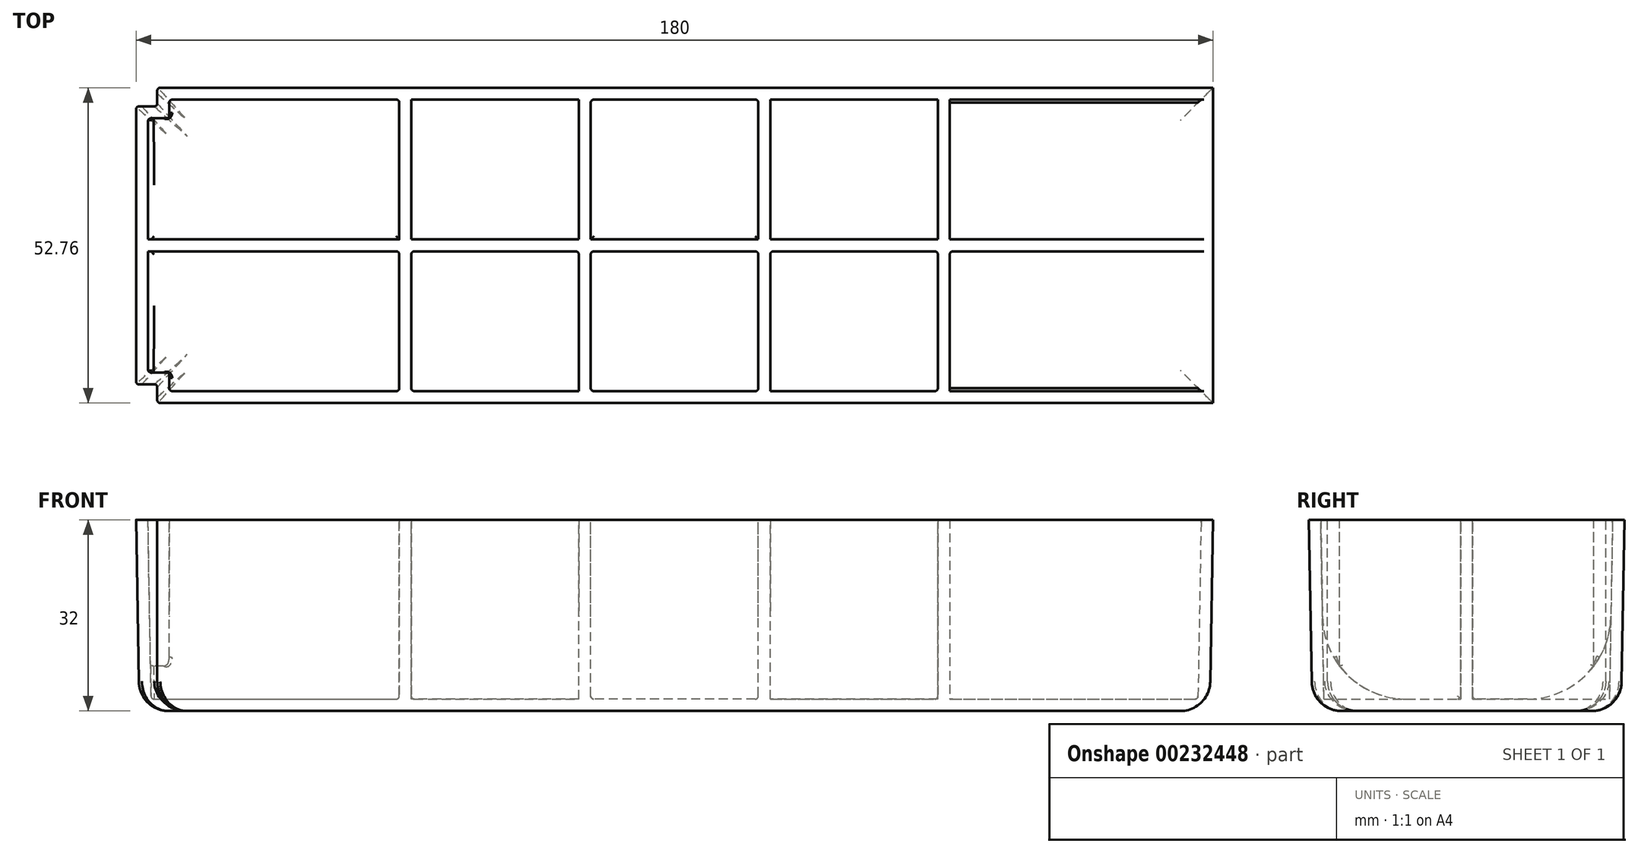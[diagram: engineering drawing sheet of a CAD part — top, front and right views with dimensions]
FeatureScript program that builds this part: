
annotation { "Feature Type Name" : "Feature", "Feature Type Description" : "" }
export const myFeature = defineFeature(function(context is Context, id is Id, definition is map)
    precondition{}
    {
        {
            var Q0;
            Q0=qCreatedBy(makeId("Top.planeOp"),FACE);
            var sketch = newSketch(context, id + "F0", { "sketchPlane" : qUnion([Q0])});
            skLineSegment(sketch, "E0.bottom", {"start": v(90, 26.38) * mm, "end": v(-90, 26.38) * mm});
            skLineSegment(sketch, "E0.top", {"start": v(90, -26.38) * mm, "end": v(-90, -26.38) * mm});
            skLineSegment(sketch, "E0.left", {"start": v(90, 26.38) * mm, "end": v(90, -26.38) * mm});
            skLineSegment(sketch, "E0.right", {"start": v(-90, 26.38) * mm, "end": v(-90, -26.38) * mm});
            skPoint(sketch, "E0.middle", {"position": v(0, 0) * mm});
            skSolve(sketch);
        }
        {
            var Q0;
            Q0=makeQuery(id+"F0.imprint","IMPRINT",FACE,{"disambiguationData":[TD([[makeQuery(id+"F0.imprint","IMPRINT",EDGE,{"derivedFrom":sQuery(id+"F0.wireOp",EDGE,"E0.bottom")}),1.0]])]});
            extrude(context, id + "F1", {"entities" : qUnion([Q0]), "oppositeDirection" : true, "depth" : 32 * mm, "hasDraft" : true, "draftAngle" : 1 * degree, "draftPullDirection" : true});
        }
        {
            var Q0;
            Q0=makeQuery(id+"F1.opExtrude","CAP_FACE",FACE,{"disambiguationData":[OSD([sQuery(id+"F0.wireOp",EDGE,"E0.bottom"),sQuery(id+"F0.wireOp",EDGE,"E0.top"),sQuery(id+"F0.wireOp",EDGE,"E0.left"),sQuery(id+"F0.wireOp",EDGE,"E0.right")])],"isStart":true});
            var sketch = newSketch(context, id + "F2", { "sketchPlane" : qUnion([Q0])});
            skLineSegment(sketch, "E1.bottom", {"start": v(-90, 23.25) * mm, "end": v(90, 23.25) * mm});
            skLineSegment(sketch, "E1.top", {"start": v(-90, -23.25) * mm, "end": v(90, -23.25) * mm});
            skLineSegment(sketch, "E1.left", {"start": v(-90, 23.25) * mm, "end": v(-90, -23.25) * mm});
            skLineSegment(sketch, "E1.right", {"start": v(90, 23.25) * mm, "end": v(90, -23.25) * mm});
            skPoint(sketch, "E1.middle", {"position": v(0, 0) * mm});
            skLineSegment(sketch, "E2.bottom", {"start": v(-86.45, 31.86) * mm, "end": v(-112.75, 31.86) * mm});
            skLineSegment(sketch, "E2.top", {"start": v(-86.45, -31.86) * mm, "end": v(-112.75, -31.86) * mm});
            skLineSegment(sketch, "E2.left", {"start": v(-86.45, 31.86) * mm, "end": v(-86.45, -31.86) * mm});
            skLineSegment(sketch, "E2.right", {"start": v(-112.75, 31.86) * mm, "end": v(-112.75, -31.86) * mm});
            skPoint(sketch, "E2.middle", {"position": v(-99.6, 0) * mm});
            skLineSegment(sketch, "E3.0", {"start": v(-90, 26.38) * mm, "end": v(-90, -26.38) * mm, "construction": true});
            skSolve(sketch);
        }
        {
            var Q0;
            {var subQ0=sQuery(id+"F2.wireOp",EDGE,"E1.bottom");var subQ3=sQuery(id+"F2.wireOp",EDGE,"E2.left");var subQ4=makeQuery(id+"F2.imprint","INTERSECT",VERTEX,{"derivedFrom":[subQ0,subQ3]});Q0=makeQuery(id+"F2.imprint","IMPRINT",FACE,{"disambiguationData":[TD([[makeQuery(id+"F2.imprint","IMPRINT",EDGE,{"disambiguationData":[TD([[subQ4,1.0]])],"derivedFrom":subQ3}),-1.0]])]});}
            var Q1;
            {var subQ0=sQuery(id+"F2.wireOp",EDGE,"E1.top");var subQ3=sQuery(id+"F2.wireOp",EDGE,"E2.left");var subQ4=makeQuery(id+"F2.imprint","INTERSECT",VERTEX,{"derivedFrom":[subQ0,subQ3]});Q1=makeQuery(id+"F2.imprint","IMPRINT",FACE,{"disambiguationData":[TD([[makeQuery(id+"F2.imprint","IMPRINT",EDGE,{"disambiguationData":[TD([[subQ4,-1.0]])],"derivedFrom":subQ3}),-1.0]])]});}
            extrude(context, id + "F3", {"entities" : qUnion([Q0, Q1]), "operationType" : NewBodyOperationType.REMOVE, "endBound" : BoundingType.THROUGH_ALL, "oppositeDirection" : true, "depth" : 25 * mm});
        }
        {
            var Q0;
            Q0=makeQuery(id+"F1.opExtrude","CAP_FACE",FACE,{"disambiguationData":[OSD([sQuery(id+"F0.wireOp",EDGE,"E0.bottom"),sQuery(id+"F0.wireOp",EDGE,"E0.top"),sQuery(id+"F0.wireOp",EDGE,"E0.left"),sQuery(id+"F0.wireOp",EDGE,"E0.right")])],"isStart":true});
            shell(context, id + "F4", {"entities" : qUnion([Q0]), "thickness" : 2 * mm});
        }
        {
            var Q0;
            Q0=makeQuery(id+"F1.opExtrude","CAP_FACE",FACE,{"disambiguationData":[OSD([sQuery(id+"F0.wireOp",EDGE,"E0.bottom"),sQuery(id+"F0.wireOp",EDGE,"E0.top"),sQuery(id+"F0.wireOp",EDGE,"E0.left"),sQuery(id+"F0.wireOp",EDGE,"E0.right")])],"isStart":false});
            fillet(context, id + "F5", {"entities" : qUnion([Q0]), "radius" : 5 * mm, "tangentPropagation" : true, "allowEdgeOverflow" : false});
        }
        {
            var Q0;
            Q0=makeQuery(id+"F1.opExtrude","CAP_FACE",FACE,{"disambiguationData":[OSD([sQuery(id+"F0.wireOp",EDGE,"E0.bottom"),sQuery(id+"F0.wireOp",EDGE,"E0.top"),sQuery(id+"F0.wireOp",EDGE,"E0.left"),sQuery(id+"F0.wireOp",EDGE,"E0.right")])],"isStart":true});
            var sketch = newSketch(context, id + "F6", { "sketchPlane" : qUnion([Q0])});
            skLineSegment(sketch, "E4", {"start": v(0, 26.38) * mm, "end": v(0, -26.38) * mm, "construction": true});
            skLineSegment(sketch, "E5.1.0.0", {"start": v(15, 26.38) * mm, "end": v(15, -26.38) * mm, "construction": true});
            skLineSegment(sketch, "E5.direction1", {"start": v(0, -26.38) * mm, "end": v(15, -26.38) * mm, "construction": true});
            skLineSegment(sketch, "E6", {"start": v(-15, 26.38) * mm, "end": v(-15, -26.38) * mm, "construction": true});
            skLineSegment(sketch, "E7.bottom", {"start": v(16, 26.38) * mm, "end": v(14, 26.38) * mm});
            skLineSegment(sketch, "E7.top", {"start": v(16, -26.38) * mm, "end": v(14, -26.38) * mm});
            skLineSegment(sketch, "E7.left", {"start": v(16, 26.38) * mm, "end": v(16, -26.38) * mm});
            skLineSegment(sketch, "E7.right", {"start": v(14, 26.38) * mm, "end": v(14, -26.38) * mm});
            skPoint(sketch, "E7.middle", {"position": v(15, 0) * mm});
            skLineSegment(sketch, "E8.bottom", {"start": v(90, -1) * mm, "end": v(-90, -1) * mm});
            skLineSegment(sketch, "E8.top", {"start": v(90, 1) * mm, "end": v(-90, 1) * mm});
            skLineSegment(sketch, "E8.left", {"start": v(90, -1) * mm, "end": v(90, 1) * mm});
            skLineSegment(sketch, "E8.right", {"start": v(-90, -1) * mm, "end": v(-90, 1) * mm});
            skPoint(sketch, "E8.middle", {"position": v(0, 0) * mm});
            skLineSegment(sketch, "E9.bottom", {"start": v(-14, 26.38) * mm, "end": v(-16, 26.38) * mm});
            skLineSegment(sketch, "E9.top", {"start": v(-14, -26.38) * mm, "end": v(-16, -26.38) * mm});
            skLineSegment(sketch, "E9.left", {"start": v(-14, 26.38) * mm, "end": v(-14, -26.38) * mm});
            skLineSegment(sketch, "E9.right", {"start": v(-16, 26.38) * mm, "end": v(-16, -26.38) * mm});
            skPoint(sketch, "E9.middle", {"position": v(-15, 0) * mm});
            skLineSegment(sketch, "E10", {"start": v(-45, 26.38) * mm, "end": v(-45, -26.38) * mm, "construction": true});
            skLineSegment(sketch, "E11", {"start": v(45, 26.38) * mm, "end": v(45, -26.38) * mm, "construction": true});
            skLineSegment(sketch, "E12.bottom", {"start": v(-44, 26.38) * mm, "end": v(-46, 26.38) * mm});
            skLineSegment(sketch, "E12.top", {"start": v(-44, -26.38) * mm, "end": v(-46, -26.38) * mm});
            skLineSegment(sketch, "E12.left", {"start": v(-44, 26.38) * mm, "end": v(-44, -26.38) * mm});
            skLineSegment(sketch, "E12.right", {"start": v(-46, 26.38) * mm, "end": v(-46, -26.38) * mm});
            skPoint(sketch, "E12.middle", {"position": v(-45, 0) * mm});
            skLineSegment(sketch, "E13.bottom", {"start": v(46, 26.38) * mm, "end": v(44, 26.38) * mm});
            skLineSegment(sketch, "E13.top", {"start": v(46, -26.38) * mm, "end": v(44, -26.38) * mm});
            skLineSegment(sketch, "E13.left", {"start": v(46, 26.38) * mm, "end": v(46, -26.38) * mm});
            skLineSegment(sketch, "E13.right", {"start": v(44, 26.38) * mm, "end": v(44, -26.38) * mm});
            skPoint(sketch, "E13.middle", {"position": v(45, 0) * mm});
            skSolve(sketch);
        }
        {
            var Q0;
            {var subQ0=sQuery(id+"F6.wireOp",EDGE,"E9.right");var subQ1=sQuery(id+"F6.wireOp",EDGE,"E8.bottom");var subQ2=makeQuery(id+"F6.imprint","INTERSECT",VERTEX,{"derivedFrom":[subQ1,subQ0]});Q0=makeQuery(id+"F6.imprint","IMPRINT",FACE,{"disambiguationData":[TD([[makeQuery(id+"F6.imprint","IMPRINT",EDGE,{"disambiguationData":[TD([[subQ2,1.0]])],"derivedFrom":subQ0}),-1.0]])]});}
            var Q1;
            {var subQ0=sQuery(id+"F6.wireOp",EDGE,"E9.left");var subQ1=sQuery(id+"F6.wireOp",EDGE,"E8.bottom");var subQ2=makeQuery(id+"F6.imprint","INTERSECT",VERTEX,{"derivedFrom":[subQ1,subQ0]});Q1=makeQuery(id+"F6.imprint","IMPRINT",FACE,{"disambiguationData":[TD([[makeQuery(id+"F6.imprint","IMPRINT",EDGE,{"disambiguationData":[TD([[subQ2,-1.0]])],"derivedFrom":subQ1}),1.0]])]});}
            var Q2;
            {var subQ0=sQuery(id+"F6.wireOp",EDGE,"E9.left");var subQ1=sQuery(id+"F6.wireOp",EDGE,"E8.bottom");var subQ2=makeQuery(id+"F6.imprint","INTERSECT",VERTEX,{"derivedFrom":[subQ1,subQ0]});Q2=makeQuery(id+"F6.imprint","IMPRINT",FACE,{"disambiguationData":[TD([[makeQuery(id+"F6.imprint","IMPRINT",EDGE,{"disambiguationData":[TD([[subQ2,-1.0]])],"derivedFrom":subQ1}),-1.0]])]});}
            var Q3;
            {var subQ0=sQuery(id+"F6.wireOp",EDGE,"E9.left");var subQ1=sQuery(id+"F6.wireOp",EDGE,"E8.top");var subQ2=makeQuery(id+"F6.imprint","INTERSECT",VERTEX,{"derivedFrom":[subQ1,subQ0]});Q3=makeQuery(id+"F6.imprint","IMPRINT",FACE,{"disambiguationData":[TD([[makeQuery(id+"F6.imprint","IMPRINT",EDGE,{"disambiguationData":[TD([[subQ2,-1.0]])],"derivedFrom":subQ1}),-1.0]])]});}
            var Q4;
            {var subQ0=sQuery(id+"F6.wireOp",EDGE,"E8.top");var subQ1=sQuery(id+"F6.wireOp",EDGE,"E7.right");var subQ2=makeQuery(id+"F6.imprint","INTERSECT",VERTEX,{"derivedFrom":[subQ1,subQ0]});Q4=makeQuery(id+"F6.imprint","IMPRINT",FACE,{"disambiguationData":[TD([[makeQuery(id+"F6.imprint","IMPRINT",EDGE,{"disambiguationData":[TD([[subQ2,-1.0]])],"derivedFrom":subQ1}),-1.0]])]});}
            var Q5;
            {var subQ0=sQuery(id+"F6.wireOp",EDGE,"E8.top");var subQ1=sQuery(id+"F6.wireOp",EDGE,"E7.left");var subQ2=makeQuery(id+"F6.imprint","INTERSECT",VERTEX,{"derivedFrom":[subQ1,subQ0]});Q5=makeQuery(id+"F6.imprint","IMPRINT",FACE,{"disambiguationData":[TD([[makeQuery(id+"F6.imprint","IMPRINT",EDGE,{"disambiguationData":[TD([[subQ2,-1.0]])],"derivedFrom":subQ1}),1.0]])]});}
            var Q6;
            {var subQ0=sQuery(id+"F6.wireOp",EDGE,"E8.top");var subQ1=sQuery(id+"F6.wireOp",EDGE,"E7.left");var subQ2=makeQuery(id+"F6.imprint","INTERSECT",VERTEX,{"derivedFrom":[subQ1,subQ0]});Q6=makeQuery(id+"F6.imprint","IMPRINT",FACE,{"disambiguationData":[TD([[makeQuery(id+"F6.imprint","IMPRINT",EDGE,{"disambiguationData":[TD([[subQ2,-1.0]])],"derivedFrom":subQ1}),-1.0]])]});}
            var Q7;
            {var subQ0=sQuery(id+"F6.wireOp",EDGE,"E8.bottom");var subQ1=sQuery(id+"F6.wireOp",EDGE,"E7.left");var subQ2=makeQuery(id+"F6.imprint","INTERSECT",VERTEX,{"derivedFrom":[subQ1,subQ0]});Q7=makeQuery(id+"F6.imprint","IMPRINT",FACE,{"disambiguationData":[TD([[makeQuery(id+"F6.imprint","IMPRINT",EDGE,{"disambiguationData":[TD([[subQ2,-1.0]])],"derivedFrom":subQ0}),1.0]])]});}
            var Q8;
            {var subQ0=sQuery(id+"F6.wireOp",EDGE,"E8.top");var subQ1=sQuery(id+"F6.wireOp",EDGE,"E7.left");var subQ2=makeQuery(id+"F6.imprint","INTERSECT",VERTEX,{"derivedFrom":[subQ1,subQ0]});Q8=makeQuery(id+"F6.imprint","IMPRINT",FACE,{"disambiguationData":[TD([[makeQuery(id+"F6.imprint","IMPRINT",EDGE,{"disambiguationData":[TD([[subQ2,-1.0]])],"derivedFrom":subQ0}),-1.0]])]});}
            var Q9;
            {var subQ0=sQuery(id+"F6.wireOp",EDGE,"E12.right");var subQ1=sQuery(id+"F6.wireOp",EDGE,"E8.bottom");var subQ2=makeQuery(id+"F6.imprint","INTERSECT",VERTEX,{"derivedFrom":[subQ1,subQ0]});Q9=makeQuery(id+"F6.imprint","IMPRINT",FACE,{"disambiguationData":[TD([[makeQuery(id+"F6.imprint","IMPRINT",EDGE,{"disambiguationData":[TD([[subQ2,1.0]])],"derivedFrom":subQ0}),-1.0]])]});}
            var Q10;
            {var subQ0=sQuery(id+"F6.wireOp",EDGE,"E12.left");var subQ1=sQuery(id+"F6.wireOp",EDGE,"E8.bottom");var subQ2=makeQuery(id+"F6.imprint","INTERSECT",VERTEX,{"derivedFrom":[subQ1,subQ0]});Q10=makeQuery(id+"F6.imprint","IMPRINT",FACE,{"disambiguationData":[TD([[makeQuery(id+"F6.imprint","IMPRINT",EDGE,{"disambiguationData":[TD([[subQ2,-1.0]])],"derivedFrom":subQ1}),-1.0]])]});}
            var Q11;
            {var subQ0=sQuery(id+"F6.wireOp",EDGE,"E12.left");var subQ1=sQuery(id+"F6.wireOp",EDGE,"E8.top");var subQ2=makeQuery(id+"F6.imprint","INTERSECT",VERTEX,{"derivedFrom":[subQ1,subQ0]});Q11=makeQuery(id+"F6.imprint","IMPRINT",FACE,{"disambiguationData":[TD([[makeQuery(id+"F6.imprint","IMPRINT",EDGE,{"disambiguationData":[TD([[subQ2,-1.0]])],"derivedFrom":subQ1}),-1.0]])]});}
            var Q12;
            {var subQ0=sQuery(id+"F6.wireOp",EDGE,"E12.left");var subQ1=sQuery(id+"F6.wireOp",EDGE,"E8.bottom");var subQ2=makeQuery(id+"F6.imprint","INTERSECT",VERTEX,{"derivedFrom":[subQ1,subQ0]});Q12=makeQuery(id+"F6.imprint","IMPRINT",FACE,{"disambiguationData":[TD([[makeQuery(id+"F6.imprint","IMPRINT",EDGE,{"disambiguationData":[TD([[subQ2,-1.0]])],"derivedFrom":subQ1}),1.0]])]});}
            var Q13;
            {var subQ0=sQuery(id+"F6.wireOp",EDGE,"E13.left");var subQ1=sQuery(id+"F6.wireOp",EDGE,"E8.bottom");var subQ2=makeQuery(id+"F6.imprint","INTERSECT",VERTEX,{"derivedFrom":[subQ1,subQ0]});Q13=makeQuery(id+"F6.imprint","IMPRINT",FACE,{"disambiguationData":[TD([[makeQuery(id+"F6.imprint","IMPRINT",EDGE,{"disambiguationData":[TD([[subQ2,1.0]])],"derivedFrom":subQ0}),1.0]])]});}
            var Q14;
            {var subQ0=sQuery(id+"F6.wireOp",EDGE,"E13.left");var subQ1=sQuery(id+"F6.wireOp",EDGE,"E8.bottom");var subQ2=makeQuery(id+"F6.imprint","INTERSECT",VERTEX,{"derivedFrom":[subQ1,subQ0]});Q14=makeQuery(id+"F6.imprint","IMPRINT",FACE,{"disambiguationData":[TD([[makeQuery(id+"F6.imprint","IMPRINT",EDGE,{"disambiguationData":[TD([[subQ2,-1.0]])],"derivedFrom":subQ1}),-1.0]])]});}
            var Q15;
            {var subQ0=sQuery(id+"F6.wireOp",EDGE,"E13.left");var subQ1=sQuery(id+"F6.wireOp",EDGE,"E8.top");var subQ2=makeQuery(id+"F6.imprint","INTERSECT",VERTEX,{"derivedFrom":[subQ1,subQ0]});Q15=makeQuery(id+"F6.imprint","IMPRINT",FACE,{"disambiguationData":[TD([[makeQuery(id+"F6.imprint","IMPRINT",EDGE,{"disambiguationData":[TD([[subQ2,-1.0]])],"derivedFrom":subQ1}),-1.0]])]});}
            var Q16;
            {var subQ0=sQuery(id+"F6.wireOp",EDGE,"E13.left");var subQ1=sQuery(id+"F6.wireOp",EDGE,"E8.bottom");var subQ2=makeQuery(id+"F6.imprint","INTERSECT",VERTEX,{"derivedFrom":[subQ1,subQ0]});Q16=makeQuery(id+"F6.imprint","IMPRINT",FACE,{"disambiguationData":[TD([[makeQuery(id+"F6.imprint","IMPRINT",EDGE,{"disambiguationData":[TD([[subQ2,-1.0]])],"derivedFrom":subQ1}),1.0]])]});}
            extrude(context, id + "F7", {"entities" : qUnion([Q0, Q1, Q2, Q3, Q4, Q5, Q6, Q7, Q8, Q9, Q10, Q11, Q12, Q13, Q14, Q15, Q16]), "operationType" : NewBodyOperationType.ADD, "endBound" : BoundingType.UP_TO_NEXT, "oppositeDirection" : true, "depth" : 25 * mm});
        }
        {
            var Q0;
            {var subQ0=sQuery(id+"F6.wireOp",EDGE,"E8.bottom");var subQ1=sQuery(id+"F0.wireOp",EDGE,"E0.right");Q0=makeQuery(id+"F7.opExtrude","TWEAK_EDGE",EDGE,{"derivedFrom":[makeQuery(id+"F4.opShell","OFFSET_FACE",FACE,{"disambiguationData":[OSD([sQuery(id+"F0.wireOp",EDGE,"E0.bottom"),sQuery(id+"F0.wireOp",EDGE,"E0.top"),sQuery(id+"F0.wireOp",EDGE,"E0.left"),subQ1])]}),makeQuery(id+"F6.imprint","IMPRINT",EDGE,{"disambiguationData":[TD([[makeQuery(id+"F6.imprint","INTERSECT",VERTEX,{"derivedFrom":[subQ0,sQuery(id+"F6.wireOp",EDGE,"E9.right")]}),-1.0]])],"derivedFrom":subQ0})]});}
            var Q1;
            {var subQ0=sQuery(id+"F6.wireOp",EDGE,"E8.bottom");Q1=makeQuery(id+"F7.opExtrude","TWEAK_EDGE",EDGE,{"derivedFrom":[makeQuery(id+"F4.opShell","OFFSET_FACE",FACE,{"disambiguationData":[OSD([sQuery(id+"F0.wireOp",EDGE,"E0.bottom"),sQuery(id+"F0.wireOp",EDGE,"E0.top"),sQuery(id+"F0.wireOp",EDGE,"E0.left"),sQuery(id+"F0.wireOp",EDGE,"E0.right")])]}),makeQuery(id+"F6.imprint","IMPRINT",EDGE,{"disambiguationData":[TD([[makeQuery(id+"F6.imprint","INTERSECT",VERTEX,{"derivedFrom":[sQuery(id+"F6.wireOp",EDGE,"E7.right"),subQ0]}),-1.0]])],"derivedFrom":subQ0})]});}
            var Q2;
            {var subQ0=sQuery(id+"F6.wireOp",EDGE,"E8.bottom");var subQ1=sQuery(id+"F0.wireOp",EDGE,"E0.left");Q2=makeQuery(id+"F7.opExtrude","TWEAK_EDGE",EDGE,{"derivedFrom":[makeQuery(id+"F4.opShell","OFFSET_FACE",FACE,{"disambiguationData":[OSD([sQuery(id+"F0.wireOp",EDGE,"E0.bottom"),sQuery(id+"F0.wireOp",EDGE,"E0.top"),subQ1,sQuery(id+"F0.wireOp",EDGE,"E0.right")])]}),makeQuery(id+"F6.imprint","IMPRINT",EDGE,{"disambiguationData":[TD([[makeQuery(id+"F6.imprint","INTERSECT",VERTEX,{"derivedFrom":[sQuery(id+"F6.wireOp",EDGE,"E7.left"),subQ0]}),1.0]])],"derivedFrom":subQ0})]});}
            var Q3;
            {var subQ0=sQuery(id+"F6.wireOp",EDGE,"E8.top");var subQ1=sQuery(id+"F0.wireOp",EDGE,"E0.left");Q3=makeQuery(id+"F7.opExtrude","TWEAK_EDGE",EDGE,{"derivedFrom":[makeQuery(id+"F4.opShell","OFFSET_FACE",FACE,{"disambiguationData":[OSD([sQuery(id+"F0.wireOp",EDGE,"E0.bottom"),sQuery(id+"F0.wireOp",EDGE,"E0.top"),subQ1,sQuery(id+"F0.wireOp",EDGE,"E0.right")])]}),makeQuery(id+"F6.imprint","IMPRINT",EDGE,{"disambiguationData":[TD([[makeQuery(id+"F6.imprint","INTERSECT",VERTEX,{"derivedFrom":[sQuery(id+"F6.wireOp",EDGE,"E7.left"),subQ0]}),1.0]])],"derivedFrom":subQ0})]});}
            var Q4;
            {var subQ0=sQuery(id+"F6.wireOp",EDGE,"E8.top");Q4=makeQuery(id+"F7.opExtrude","TWEAK_EDGE",EDGE,{"derivedFrom":[makeQuery(id+"F4.opShell","OFFSET_FACE",FACE,{"disambiguationData":[OSD([sQuery(id+"F0.wireOp",EDGE,"E0.bottom"),sQuery(id+"F0.wireOp",EDGE,"E0.top"),sQuery(id+"F0.wireOp",EDGE,"E0.left"),sQuery(id+"F0.wireOp",EDGE,"E0.right")])]}),makeQuery(id+"F6.imprint","IMPRINT",EDGE,{"disambiguationData":[TD([[makeQuery(id+"F6.imprint","INTERSECT",VERTEX,{"derivedFrom":[sQuery(id+"F6.wireOp",EDGE,"E7.right"),subQ0]}),-1.0]])],"derivedFrom":subQ0})]});}
            var Q5;
            {var subQ0=sQuery(id+"F6.wireOp",EDGE,"E8.top");var subQ1=sQuery(id+"F0.wireOp",EDGE,"E0.right");Q5=makeQuery(id+"F7.opExtrude","TWEAK_EDGE",EDGE,{"derivedFrom":[makeQuery(id+"F4.opShell","OFFSET_FACE",FACE,{"disambiguationData":[OSD([sQuery(id+"F0.wireOp",EDGE,"E0.bottom"),sQuery(id+"F0.wireOp",EDGE,"E0.top"),sQuery(id+"F0.wireOp",EDGE,"E0.left"),subQ1])]}),makeQuery(id+"F6.imprint","IMPRINT",EDGE,{"disambiguationData":[TD([[makeQuery(id+"F6.imprint","INTERSECT",VERTEX,{"derivedFrom":[subQ0,sQuery(id+"F6.wireOp",EDGE,"E9.right")]}),-1.0]])],"derivedFrom":subQ0})]});}
            var Q6;
            {var subQ0=sQuery(id+"F6.wireOp",EDGE,"E8.top");var subQ1=sQuery(id+"F0.wireOp",EDGE,"E0.right");Q6=makeQuery(id+"F7.opExtrude","TWEAK_EDGE",EDGE,{"derivedFrom":[makeQuery(id+"F4.opShell","OFFSET_FACE",FACE,{"disambiguationData":[OSD([sQuery(id+"F0.wireOp",EDGE,"E0.bottom"),sQuery(id+"F0.wireOp",EDGE,"E0.top"),sQuery(id+"F0.wireOp",EDGE,"E0.left"),subQ1])]}),makeQuery(id+"F6.imprint","IMPRINT",EDGE,{"disambiguationData":[TD([[makeQuery(id+"F6.imprint","INTERSECT",VERTEX,{"derivedFrom":[subQ0,sQuery(id+"F6.wireOp",EDGE,"E12.right")]}),-1.0]])],"derivedFrom":subQ0})]});}
            var Q7;
            {var subQ0=sQuery(id+"F6.wireOp",EDGE,"E8.top");var subQ1=sQuery(id+"F0.wireOp",EDGE,"E0.left");Q7=makeQuery(id+"F7.opExtrude","TWEAK_EDGE",EDGE,{"derivedFrom":[makeQuery(id+"F4.opShell","OFFSET_FACE",FACE,{"disambiguationData":[OSD([sQuery(id+"F0.wireOp",EDGE,"E0.bottom"),sQuery(id+"F0.wireOp",EDGE,"E0.top"),subQ1,sQuery(id+"F0.wireOp",EDGE,"E0.right")])]}),makeQuery(id+"F6.imprint","IMPRINT",EDGE,{"disambiguationData":[TD([[makeQuery(id+"F6.imprint","INTERSECT",VERTEX,{"derivedFrom":[subQ0,sQuery(id+"F6.wireOp",EDGE,"E13.left")]}),1.0]])],"derivedFrom":subQ0})]});}
            var Q8;
            {var subQ0=sQuery(id+"F6.wireOp",EDGE,"E8.bottom");var subQ1=sQuery(id+"F0.wireOp",EDGE,"E0.left");Q8=makeQuery(id+"F7.opExtrude","TWEAK_EDGE",EDGE,{"derivedFrom":[makeQuery(id+"F4.opShell","OFFSET_FACE",FACE,{"disambiguationData":[OSD([sQuery(id+"F0.wireOp",EDGE,"E0.bottom"),sQuery(id+"F0.wireOp",EDGE,"E0.top"),subQ1,sQuery(id+"F0.wireOp",EDGE,"E0.right")])]}),makeQuery(id+"F6.imprint","IMPRINT",EDGE,{"disambiguationData":[TD([[makeQuery(id+"F6.imprint","INTERSECT",VERTEX,{"derivedFrom":[subQ0,sQuery(id+"F6.wireOp",EDGE,"E13.left")]}),1.0]])],"derivedFrom":subQ0})]});}
            var Q9;
            {var subQ0=sQuery(id+"F6.wireOp",EDGE,"E8.bottom");var subQ1=sQuery(id+"F0.wireOp",EDGE,"E0.right");Q9=makeQuery(id+"F7.opExtrude","TWEAK_EDGE",EDGE,{"derivedFrom":[makeQuery(id+"F4.opShell","OFFSET_FACE",FACE,{"disambiguationData":[OSD([sQuery(id+"F0.wireOp",EDGE,"E0.bottom"),sQuery(id+"F0.wireOp",EDGE,"E0.top"),sQuery(id+"F0.wireOp",EDGE,"E0.left"),subQ1])]}),makeQuery(id+"F6.imprint","IMPRINT",EDGE,{"disambiguationData":[TD([[makeQuery(id+"F6.imprint","INTERSECT",VERTEX,{"derivedFrom":[subQ0,sQuery(id+"F6.wireOp",EDGE,"E12.right")]}),-1.0]])],"derivedFrom":subQ0})]});}
            var Q10;
            {var subQ0=sQuery(id+"F2.wireOp",EDGE,"E2.left");var subQ1=sQuery(id+"F0.wireOp",EDGE,"E0.bottom");Q10=makeQuery(id+"F7.boolean.opBoolean","SPLIT",EDGE,{"disambiguationData":[TD([makeQuery(id+"F4.opShell","OFFSET_FACE",FACE,{"disambiguationData":[OSD([subQ0]),TDD([makeQuery(id+"F3.boolean.opBoolean","COPY",FACE,{"derivedFrom":makeQuery(id+"F3.opExtrude","SWEPT_FACE",FACE,{"disambiguationData":[OSD([subQ0]),TDD([makeQuery(id+"F2.imprint","IMPRINT",EDGE,{"disambiguationData":[TD([[makeQuery(id+"F2.imprint","INTERSECT",VERTEX,{"derivedFrom":[sQuery(id+"F2.wireOp",EDGE,"E1.bottom"),subQ0]}),1.0]])],"derivedFrom":subQ0})])]})})])]})])],"derivedFrom":makeQuery(id+"F4.opShell","OFFSET_EDGE",EDGE,{"disambiguationData":[OSD([subQ1]),TDD([makeQuery(id+"F1.opExtrude","CAP_EDGE",EDGE,{"disambiguationData":[OSD([subQ1])],"isStart":false})])]})});}
            var Q11;
            {var subQ0=sQuery(id+"F0.wireOp",EDGE,"E0.bottom");var subQ1=sQuery(id+"F6.wireOp",EDGE,"E9.right");var subQ2=sQuery(id+"F6.wireOp",EDGE,"E8.top");Q11=makeQuery(id+"F7.boolean.opBoolean","SPLIT",EDGE,{"disambiguationData":[TD([makeQuery(id+"F7.opExtrude","SWEPT_FACE",FACE,{"disambiguationData":[OSD([subQ1]),TDD([makeQuery(id+"F6.imprint","IMPRINT",EDGE,{"disambiguationData":[TD([[makeQuery(id+"F6.imprint","INTERSECT",VERTEX,{"derivedFrom":[subQ2,subQ1]}),1.0]])],"derivedFrom":subQ1})])]})])],"derivedFrom":makeQuery(id+"F4.opShell","OFFSET_EDGE",EDGE,{"disambiguationData":[OSD([subQ0]),TDD([makeQuery(id+"F1.opExtrude","CAP_EDGE",EDGE,{"disambiguationData":[OSD([subQ0])],"isStart":false})])]})});}
            var Q12;
            {var subQ0=sQuery(id+"F0.wireOp",EDGE,"E0.bottom");var subQ1=sQuery(id+"F6.wireOp",EDGE,"E8.top");var subQ2=sQuery(id+"F6.wireOp",EDGE,"E7.right");Q12=makeQuery(id+"F7.boolean.opBoolean","SPLIT",EDGE,{"disambiguationData":[TD([makeQuery(id+"F7.opExtrude","SWEPT_FACE",FACE,{"disambiguationData":[OSD([subQ2]),TDD([makeQuery(id+"F6.imprint","IMPRINT",EDGE,{"disambiguationData":[TD([[makeQuery(id+"F6.imprint","INTERSECT",VERTEX,{"derivedFrom":[subQ2,subQ1]}),1.0]])],"derivedFrom":subQ2})])]})])],"derivedFrom":makeQuery(id+"F4.opShell","OFFSET_EDGE",EDGE,{"disambiguationData":[OSD([subQ0]),TDD([makeQuery(id+"F1.opExtrude","CAP_EDGE",EDGE,{"disambiguationData":[OSD([subQ0])],"isStart":false})])]})});}
            var Q13;
            {var subQ0=sQuery(id+"F0.wireOp",EDGE,"E0.bottom");var subQ1=sQuery(id+"F6.wireOp",EDGE,"E8.top");var subQ2=sQuery(id+"F6.wireOp",EDGE,"E7.left");Q13=makeQuery(id+"F7.boolean.opBoolean","SPLIT",EDGE,{"disambiguationData":[TD([makeQuery(id+"F7.opExtrude","SWEPT_FACE",FACE,{"disambiguationData":[OSD([subQ2]),TDD([makeQuery(id+"F6.imprint","IMPRINT",EDGE,{"disambiguationData":[TD([[makeQuery(id+"F6.imprint","INTERSECT",VERTEX,{"derivedFrom":[subQ2,subQ1]}),1.0]])],"derivedFrom":subQ2})])]})])],"derivedFrom":makeQuery(id+"F4.opShell","OFFSET_EDGE",EDGE,{"disambiguationData":[OSD([subQ0]),TDD([makeQuery(id+"F1.opExtrude","CAP_EDGE",EDGE,{"disambiguationData":[OSD([subQ0])],"isStart":false})])]})});}
            var Q14;
            {var subQ0=sQuery(id+"F2.wireOp",EDGE,"E2.left");var subQ1=sQuery(id+"F0.wireOp",EDGE,"E0.bottom");Q14=makeQuery(id+"F7.boolean.opBoolean","SPLIT",EDGE,{"disambiguationData":[TD([makeQuery(id+"F4.opShell","OFFSET_FACE",FACE,{"disambiguationData":[OSD([subQ0]),TDD([makeQuery(id+"Fj79t6Fnd16a4gd_1.1.F3.boolean.opBoolean","COPY",FACE,{"derivedFrom":makeQuery(id+"Fj79t6Fnd16a4gd_1.1.F3.opExtrude","SWEPT_FACE",FACE,{"disambiguationData":[OSD([subQ0]),TDD([makeQuery(id+"F2.imprint","IMPRINT",EDGE,{"disambiguationData":[TD([[makeQuery(id+"F2.imprint","INTERSECT",VERTEX,{"derivedFrom":[sQuery(id+"F2.wireOp",EDGE,"E1.bottom"),subQ0]}),1.0]])],"derivedFrom":subQ0})])]})})])]})])],"derivedFrom":makeQuery(id+"F4.opShell","OFFSET_EDGE",EDGE,{"disambiguationData":[OSD([subQ1]),TDD([makeQuery(id+"F1.opExtrude","CAP_EDGE",EDGE,{"disambiguationData":[OSD([subQ1])],"isStart":false})])]})});}
            var Q15;
            {var subQ0=sQuery(id+"F2.wireOp",EDGE,"E2.left");var subQ1=sQuery(id+"F0.wireOp",EDGE,"E0.top");Q15=makeQuery(id+"F7.boolean.opBoolean","SPLIT",EDGE,{"disambiguationData":[TD([makeQuery(id+"F4.opShell","OFFSET_FACE",FACE,{"disambiguationData":[OSD([subQ0]),TDD([makeQuery(id+"Fj79t6Fnd16a4gd_1.1.F3.boolean.opBoolean","COPY",FACE,{"derivedFrom":makeQuery(id+"Fj79t6Fnd16a4gd_1.1.F3.opExtrude","SWEPT_FACE",FACE,{"disambiguationData":[OSD([subQ0]),TDD([makeQuery(id+"F2.imprint","IMPRINT",EDGE,{"disambiguationData":[TD([[makeQuery(id+"F2.imprint","INTERSECT",VERTEX,{"derivedFrom":[sQuery(id+"F2.wireOp",EDGE,"E1.top"),subQ0]}),-1.0]])],"derivedFrom":subQ0})])]})})])]})])],"derivedFrom":makeQuery(id+"F4.opShell","OFFSET_EDGE",EDGE,{"disambiguationData":[OSD([subQ1]),TDD([makeQuery(id+"F1.opExtrude","CAP_EDGE",EDGE,{"disambiguationData":[OSD([subQ1])],"isStart":false})])]})});}
            var Q16;
            {var subQ0=sQuery(id+"F0.wireOp",EDGE,"E0.top");var subQ1=sQuery(id+"F6.wireOp",EDGE,"E8.bottom");var subQ2=sQuery(id+"F6.wireOp",EDGE,"E7.left");Q16=makeQuery(id+"F7.boolean.opBoolean","SPLIT",EDGE,{"disambiguationData":[TD([makeQuery(id+"F7.opExtrude","SWEPT_FACE",FACE,{"disambiguationData":[OSD([subQ2]),TDD([makeQuery(id+"F6.imprint","IMPRINT",EDGE,{"disambiguationData":[TD([[makeQuery(id+"F6.imprint","INTERSECT",VERTEX,{"derivedFrom":[subQ2,subQ1]}),-1.0]])],"derivedFrom":subQ2})])]})])],"derivedFrom":makeQuery(id+"F4.opShell","OFFSET_EDGE",EDGE,{"disambiguationData":[OSD([subQ0]),TDD([makeQuery(id+"F1.opExtrude","CAP_EDGE",EDGE,{"disambiguationData":[OSD([subQ0])],"isStart":false})])]})});}
            var Q17;
            {var subQ0=sQuery(id+"F0.wireOp",EDGE,"E0.top");var subQ1=sQuery(id+"F6.wireOp",EDGE,"E8.bottom");var subQ2=sQuery(id+"F6.wireOp",EDGE,"E7.right");Q17=makeQuery(id+"F7.boolean.opBoolean","SPLIT",EDGE,{"disambiguationData":[TD([makeQuery(id+"F7.opExtrude","SWEPT_FACE",FACE,{"disambiguationData":[OSD([subQ2]),TDD([makeQuery(id+"F6.imprint","IMPRINT",EDGE,{"disambiguationData":[TD([[makeQuery(id+"F6.imprint","INTERSECT",VERTEX,{"derivedFrom":[subQ2,subQ1]}),-1.0]])],"derivedFrom":subQ2})])]})])],"derivedFrom":makeQuery(id+"F4.opShell","OFFSET_EDGE",EDGE,{"disambiguationData":[OSD([subQ0]),TDD([makeQuery(id+"F1.opExtrude","CAP_EDGE",EDGE,{"disambiguationData":[OSD([subQ0])],"isStart":false})])]})});}
            var Q18;
            {var subQ0=sQuery(id+"F0.wireOp",EDGE,"E0.top");var subQ2=sQuery(id+"F6.wireOp",EDGE,"E8.bottom");var subQ4=sQuery(id+"F6.wireOp",EDGE,"E9.right");Q18=makeQuery(id+"F7.boolean.opBoolean","SPLIT",EDGE,{"disambiguationData":[TD([makeQuery(id+"F7.opExtrude","SWEPT_FACE",FACE,{"disambiguationData":[OSD([subQ4]),TDD([makeQuery(id+"F6.imprint","IMPRINT",EDGE,{"disambiguationData":[TD([[makeQuery(id+"F6.imprint","INTERSECT",VERTEX,{"derivedFrom":[subQ2,subQ4]}),-1.0]])],"derivedFrom":subQ4})])]})])],"derivedFrom":makeQuery(id+"F4.opShell","OFFSET_EDGE",EDGE,{"disambiguationData":[OSD([subQ0]),TDD([makeQuery(id+"F1.opExtrude","CAP_EDGE",EDGE,{"disambiguationData":[OSD([subQ0])],"isStart":false})])]})});}
            var Q19;
            {var subQ0=sQuery(id+"F2.wireOp",EDGE,"E2.left");var subQ1=sQuery(id+"F0.wireOp",EDGE,"E0.top");Q19=makeQuery(id+"F7.boolean.opBoolean","SPLIT",EDGE,{"disambiguationData":[TD([makeQuery(id+"F4.opShell","OFFSET_FACE",FACE,{"disambiguationData":[OSD([subQ0]),TDD([makeQuery(id+"F3.boolean.opBoolean","COPY",FACE,{"derivedFrom":makeQuery(id+"F3.opExtrude","SWEPT_FACE",FACE,{"disambiguationData":[OSD([subQ0]),TDD([makeQuery(id+"F2.imprint","IMPRINT",EDGE,{"disambiguationData":[TD([[makeQuery(id+"F2.imprint","INTERSECT",VERTEX,{"derivedFrom":[sQuery(id+"F2.wireOp",EDGE,"E1.top"),subQ0]}),-1.0]])],"derivedFrom":subQ0})])]})})])]})])],"derivedFrom":makeQuery(id+"F4.opShell","OFFSET_EDGE",EDGE,{"disambiguationData":[OSD([subQ1]),TDD([makeQuery(id+"F1.opExtrude","CAP_EDGE",EDGE,{"disambiguationData":[OSD([subQ1])],"isStart":false})])]})});}
            fillet(context, id + "F8", {"entities" : qUnion([Q0, Q1, Q2, Q3, Q4, Q5, Q6, Q7, Q8, Q9, Q10, Q11, Q12, Q13, Q14, Q15, Q16, Q17, Q18, Q19]), "radius" : 14 * mm, "tangentPropagation" : true, "allowEdgeOverflow" : false});
        }
        {
            var Q0;
            {var subQ0=sQuery(id+"F2.wireOp",EDGE,"E2.left");var subQ1=sQuery(id+"F0.wireOp",EDGE,"E0.bottom");Q0=makeQuery(id+"F3.boolean.opBoolean","INTERSECT",EDGE,{"derivedFrom":[makeQuery(id+"F1.opExtrude","SWEPT_FACE",FACE,{"disambiguationData":[OSD([subQ1])]}),makeQuery(id+"F3.opExtrude","SWEPT_FACE",FACE,{"disambiguationData":[OSD([subQ0]),TDD([makeQuery(id+"F2.imprint","IMPRINT",EDGE,{"disambiguationData":[TD([[makeQuery(id+"F2.imprint","INTERSECT",VERTEX,{"derivedFrom":[sQuery(id+"F2.wireOp",EDGE,"E1.bottom"),subQ0]}),1.0]])],"derivedFrom":subQ0})])]})]});}
            var Q1;
            Q1=makeQuery(id+"F3.boolean.opBoolean","COPY",EDGE,{"derivedFrom":makeQuery(id+"F3.opExtrude","SWEPT_EDGE",EDGE,{"disambiguationData":[OSD([sQuery(id+"F2.wireOp",EDGE,"E1.bottom"),sQuery(id+"F2.wireOp",EDGE,"E2.left")])]})});
            var Q2;
            Q2=makeQuery(id+"F3.boolean.opBoolean","INTERSECT",EDGE,{"derivedFrom":[makeQuery(id+"F1.opExtrude","SWEPT_FACE",FACE,{"disambiguationData":[OSD([sQuery(id+"F0.wireOp",EDGE,"E0.right")])]}),makeQuery(id+"F3.opExtrude","SWEPT_FACE",FACE,{"disambiguationData":[OSD([sQuery(id+"F2.wireOp",EDGE,"E1.bottom")])]})]});
            var Q3;
            {var subQ0=sQuery(id+"F2.wireOp",EDGE,"E2.left");var subQ1=sQuery(id+"F0.wireOp",EDGE,"E0.top");Q3=makeQuery(id+"F3.boolean.opBoolean","INTERSECT",EDGE,{"derivedFrom":[makeQuery(id+"F1.opExtrude","SWEPT_FACE",FACE,{"disambiguationData":[OSD([subQ1])]}),makeQuery(id+"F3.opExtrude","SWEPT_FACE",FACE,{"disambiguationData":[OSD([subQ0]),TDD([makeQuery(id+"F2.imprint","IMPRINT",EDGE,{"disambiguationData":[TD([[makeQuery(id+"F2.imprint","INTERSECT",VERTEX,{"derivedFrom":[sQuery(id+"F2.wireOp",EDGE,"E1.top"),subQ0]}),-1.0]])],"derivedFrom":subQ0})])]})]});}
            var Q4;
            Q4=makeQuery(id+"F3.boolean.opBoolean","INTERSECT",EDGE,{"derivedFrom":[makeQuery(id+"F1.opExtrude","SWEPT_FACE",FACE,{"disambiguationData":[OSD([sQuery(id+"F0.wireOp",EDGE,"E0.right")])]}),makeQuery(id+"F3.opExtrude","SWEPT_FACE",FACE,{"disambiguationData":[OSD([sQuery(id+"F2.wireOp",EDGE,"E1.top")])]})]});
            var Q5;
            Q5=makeQuery(id+"F3.boolean.opBoolean","COPY",EDGE,{"derivedFrom":makeQuery(id+"F3.opExtrude","SWEPT_EDGE",EDGE,{"disambiguationData":[OSD([sQuery(id+"F2.wireOp",EDGE,"E1.top"),sQuery(id+"F2.wireOp",EDGE,"E2.left")])]})});
            var Q6;
            Q6=makeQuery(id+"Fj79t6Fnd16a4gd_1.1.F3.boolean.opBoolean","INTERSECT",EDGE,{"derivedFrom":[makeQuery(id+"F1.opExtrude","SWEPT_FACE",FACE,{"disambiguationData":[OSD([sQuery(id+"F0.wireOp",EDGE,"E0.left")])]}),makeQuery(id+"Fj79t6Fnd16a4gd_1.1.F3.opExtrude","SWEPT_FACE",FACE,{"disambiguationData":[OSD([sQuery(id+"F2.wireOp",EDGE,"E1.top")])]})]});
            var Q7;
            Q7=makeQuery(id+"Fj79t6Fnd16a4gd_1.1.F3.boolean.opBoolean","COPY",EDGE,{"derivedFrom":makeQuery(id+"Fj79t6Fnd16a4gd_1.1.F3.opExtrude","SWEPT_EDGE",EDGE,{"disambiguationData":[OSD([sQuery(id+"F2.wireOp",EDGE,"E1.top"),sQuery(id+"F2.wireOp",EDGE,"E2.left")])]})});
            var Q8;
            {var subQ0=sQuery(id+"F2.wireOp",EDGE,"E2.left");var subQ1=sQuery(id+"F0.wireOp",EDGE,"E0.top");Q8=makeQuery(id+"Fj79t6Fnd16a4gd_1.1.F3.boolean.opBoolean","INTERSECT",EDGE,{"derivedFrom":[makeQuery(id+"F1.opExtrude","SWEPT_FACE",FACE,{"disambiguationData":[OSD([subQ1])]}),makeQuery(id+"Fj79t6Fnd16a4gd_1.1.F3.opExtrude","SWEPT_FACE",FACE,{"disambiguationData":[OSD([subQ0]),TDD([makeQuery(id+"F2.imprint","IMPRINT",EDGE,{"disambiguationData":[TD([[makeQuery(id+"F2.imprint","INTERSECT",VERTEX,{"derivedFrom":[sQuery(id+"F2.wireOp",EDGE,"E1.top"),subQ0]}),-1.0]])],"derivedFrom":subQ0})])]})]});}
            var Q9;
            {var subQ0=sQuery(id+"F2.wireOp",EDGE,"E2.left");var subQ1=sQuery(id+"F0.wireOp",EDGE,"E0.bottom");Q9=makeQuery(id+"Fj79t6Fnd16a4gd_1.1.F3.boolean.opBoolean","INTERSECT",EDGE,{"derivedFrom":[makeQuery(id+"F1.opExtrude","SWEPT_FACE",FACE,{"disambiguationData":[OSD([subQ1])]}),makeQuery(id+"Fj79t6Fnd16a4gd_1.1.F3.opExtrude","SWEPT_FACE",FACE,{"disambiguationData":[OSD([subQ0]),TDD([makeQuery(id+"F2.imprint","IMPRINT",EDGE,{"disambiguationData":[TD([[makeQuery(id+"F2.imprint","INTERSECT",VERTEX,{"derivedFrom":[sQuery(id+"F2.wireOp",EDGE,"E1.bottom"),subQ0]}),1.0]])],"derivedFrom":subQ0})])]})]});}
            var Q10;
            Q10=makeQuery(id+"Fj79t6Fnd16a4gd_1.1.F3.boolean.opBoolean","COPY",EDGE,{"derivedFrom":makeQuery(id+"Fj79t6Fnd16a4gd_1.1.F3.opExtrude","SWEPT_EDGE",EDGE,{"disambiguationData":[OSD([sQuery(id+"F2.wireOp",EDGE,"E1.bottom"),sQuery(id+"F2.wireOp",EDGE,"E2.left")])]})});
            var Q11;
            Q11=makeQuery(id+"Fj79t6Fnd16a4gd_1.1.F3.boolean.opBoolean","INTERSECT",EDGE,{"derivedFrom":[makeQuery(id+"F1.opExtrude","SWEPT_FACE",FACE,{"disambiguationData":[OSD([sQuery(id+"F0.wireOp",EDGE,"E0.left")])]}),makeQuery(id+"Fj79t6Fnd16a4gd_1.1.F3.opExtrude","SWEPT_FACE",FACE,{"disambiguationData":[OSD([sQuery(id+"F2.wireOp",EDGE,"E1.bottom")])]})]});
            var Q12;
            {var subQ0=sQuery(id+"F2.wireOp",EDGE,"E2.left");var subQ1=sQuery(id+"F0.wireOp",EDGE,"E0.bottom");Q12=makeQuery(id+"F4.opShell","OFFSET_EDGE",EDGE,{"disambiguationData":[OSD([subQ1,subQ0]),TDD([makeQuery(id+"F3.boolean.opBoolean","INTERSECT",EDGE,{"derivedFrom":[makeQuery(id+"F1.opExtrude","SWEPT_FACE",FACE,{"disambiguationData":[OSD([subQ1])]}),makeQuery(id+"F3.opExtrude","SWEPT_FACE",FACE,{"disambiguationData":[OSD([subQ0]),TDD([makeQuery(id+"F2.imprint","IMPRINT",EDGE,{"disambiguationData":[TD([[makeQuery(id+"F2.imprint","INTERSECT",VERTEX,{"derivedFrom":[sQuery(id+"F2.wireOp",EDGE,"E1.bottom"),subQ0]}),1.0]])],"derivedFrom":subQ0})])]})]})])]});}
            var Q13;
            {var subQ0=sQuery(id+"F2.wireOp",EDGE,"E2.left");var subQ1=sQuery(id+"F2.wireOp",EDGE,"E1.bottom");Q13=makeQuery(id+"F4.opShell","OFFSET_EDGE",EDGE,{"disambiguationData":[OSD([subQ1,subQ0]),TDD([makeQuery(id+"F3.boolean.opBoolean","COPY",EDGE,{"derivedFrom":makeQuery(id+"F3.opExtrude","SWEPT_EDGE",EDGE,{"disambiguationData":[OSD([subQ1,subQ0])]})})])]});}
            var Q14;
            Q14=makeQuery(id+"F4.opShell","OFFSET_EDGE",EDGE,{"disambiguationData":[OSD([sQuery(id+"F0.wireOp",EDGE,"E0.right"),sQuery(id+"F2.wireOp",EDGE,"E1.bottom")])]});
            var Q15;
            {var subQ0=sQuery(id+"F2.wireOp",EDGE,"E2.left");var subQ1=sQuery(id+"F0.wireOp",EDGE,"E0.bottom");Q15=makeQuery(id+"F4.opShell","OFFSET_EDGE",EDGE,{"disambiguationData":[OSD([subQ1,subQ0]),TDD([makeQuery(id+"Fj79t6Fnd16a4gd_1.1.F3.boolean.opBoolean","INTERSECT",EDGE,{"derivedFrom":[makeQuery(id+"F1.opExtrude","SWEPT_FACE",FACE,{"disambiguationData":[OSD([subQ1])]}),makeQuery(id+"Fj79t6Fnd16a4gd_1.1.F3.opExtrude","SWEPT_FACE",FACE,{"disambiguationData":[OSD([subQ0]),TDD([makeQuery(id+"F2.imprint","IMPRINT",EDGE,{"disambiguationData":[TD([[makeQuery(id+"F2.imprint","INTERSECT",VERTEX,{"derivedFrom":[sQuery(id+"F2.wireOp",EDGE,"E1.bottom"),subQ0]}),1.0]])],"derivedFrom":subQ0})])]})]})])]});}
            var Q16;
            {var subQ0=sQuery(id+"F2.wireOp",EDGE,"E2.left");var subQ1=sQuery(id+"F2.wireOp",EDGE,"E1.bottom");Q16=makeQuery(id+"F4.opShell","OFFSET_EDGE",EDGE,{"disambiguationData":[OSD([subQ1,subQ0]),TDD([makeQuery(id+"Fj79t6Fnd16a4gd_1.1.F3.boolean.opBoolean","COPY",EDGE,{"derivedFrom":makeQuery(id+"Fj79t6Fnd16a4gd_1.1.F3.opExtrude","SWEPT_EDGE",EDGE,{"disambiguationData":[OSD([subQ1,subQ0])]})})])]});}
            var Q17;
            Q17=makeQuery(id+"F4.opShell","OFFSET_EDGE",EDGE,{"disambiguationData":[OSD([sQuery(id+"F0.wireOp",EDGE,"E0.left"),sQuery(id+"F2.wireOp",EDGE,"E1.bottom")])]});
            var Q18;
            Q18=makeQuery(id+"F4.opShell","OFFSET_EDGE",EDGE,{"disambiguationData":[OSD([sQuery(id+"F0.wireOp",EDGE,"E0.left"),sQuery(id+"F2.wireOp",EDGE,"E1.top")])]});
            var Q19;
            {var subQ0=sQuery(id+"F2.wireOp",EDGE,"E2.left");var subQ1=sQuery(id+"F2.wireOp",EDGE,"E1.top");Q19=makeQuery(id+"F4.opShell","OFFSET_EDGE",EDGE,{"disambiguationData":[OSD([subQ1,subQ0]),TDD([makeQuery(id+"Fj79t6Fnd16a4gd_1.1.F3.boolean.opBoolean","COPY",EDGE,{"derivedFrom":makeQuery(id+"Fj79t6Fnd16a4gd_1.1.F3.opExtrude","SWEPT_EDGE",EDGE,{"disambiguationData":[OSD([subQ1,subQ0])]})})])]});}
            var Q20;
            {var subQ0=sQuery(id+"F2.wireOp",EDGE,"E2.left");var subQ1=sQuery(id+"F0.wireOp",EDGE,"E0.top");Q20=makeQuery(id+"F4.opShell","OFFSET_EDGE",EDGE,{"disambiguationData":[OSD([subQ1,subQ0]),TDD([makeQuery(id+"Fj79t6Fnd16a4gd_1.1.F3.boolean.opBoolean","INTERSECT",EDGE,{"derivedFrom":[makeQuery(id+"F1.opExtrude","SWEPT_FACE",FACE,{"disambiguationData":[OSD([subQ1])]}),makeQuery(id+"Fj79t6Fnd16a4gd_1.1.F3.opExtrude","SWEPT_FACE",FACE,{"disambiguationData":[OSD([subQ0]),TDD([makeQuery(id+"F2.imprint","IMPRINT",EDGE,{"disambiguationData":[TD([[makeQuery(id+"F2.imprint","INTERSECT",VERTEX,{"derivedFrom":[sQuery(id+"F2.wireOp",EDGE,"E1.top"),subQ0]}),-1.0]])],"derivedFrom":subQ0})])]})]})])]});}
            var Q21;
            Q21=makeQuery(id+"F4.opShell","OFFSET_EDGE",EDGE,{"disambiguationData":[OSD([sQuery(id+"F0.wireOp",EDGE,"E0.right"),sQuery(id+"F2.wireOp",EDGE,"E1.top")])]});
            var Q22;
            {var subQ0=sQuery(id+"F2.wireOp",EDGE,"E2.left");var subQ1=sQuery(id+"F2.wireOp",EDGE,"E1.top");Q22=makeQuery(id+"F4.opShell","OFFSET_EDGE",EDGE,{"disambiguationData":[OSD([subQ1,subQ0]),TDD([makeQuery(id+"F3.boolean.opBoolean","COPY",EDGE,{"derivedFrom":makeQuery(id+"F3.opExtrude","SWEPT_EDGE",EDGE,{"disambiguationData":[OSD([subQ1,subQ0])]})})])]});}
            var Q23;
            {var subQ0=sQuery(id+"F2.wireOp",EDGE,"E2.left");var subQ1=sQuery(id+"F0.wireOp",EDGE,"E0.top");Q23=makeQuery(id+"F4.opShell","OFFSET_EDGE",EDGE,{"disambiguationData":[OSD([subQ1,subQ0]),TDD([makeQuery(id+"F3.boolean.opBoolean","INTERSECT",EDGE,{"derivedFrom":[makeQuery(id+"F1.opExtrude","SWEPT_FACE",FACE,{"disambiguationData":[OSD([subQ1])]}),makeQuery(id+"F3.opExtrude","SWEPT_FACE",FACE,{"disambiguationData":[OSD([subQ0]),TDD([makeQuery(id+"F2.imprint","IMPRINT",EDGE,{"disambiguationData":[TD([[makeQuery(id+"F2.imprint","INTERSECT",VERTEX,{"derivedFrom":[sQuery(id+"F2.wireOp",EDGE,"E1.top"),subQ0]}),-1.0]])],"derivedFrom":subQ0})])]})]})])]});}
            var Q24;
            {var subQ0=sQuery(id+"F0.wireOp",EDGE,"E0.bottom");var subQ2=sQuery(id+"F2.wireOp",EDGE,"E1.bottom");var subQ4=sQuery(id+"F0.wireOp",EDGE,"E0.right");Q24=makeQuery(id+"F7.boolean.opBoolean","SPLIT",FACE,{"disambiguationData":[TD([makeQuery(id+"F4.opShell","OFFSET_FACE",FACE,{"disambiguationData":[OSD([subQ2]),TDD([makeQuery(id+"F3.boolean.opBoolean","COPY",FACE,{"derivedFrom":makeQuery(id+"F3.opExtrude","SWEPT_FACE",FACE,{"disambiguationData":[OSD([subQ2])]})})])]})])],"derivedFrom":makeQuery(id+"F4.opShell","OFFSET_FACE",FACE,{"disambiguationData":[OSD([subQ0,sQuery(id+"F0.wireOp",EDGE,"E0.top"),sQuery(id+"F0.wireOp",EDGE,"E0.left"),subQ4])]})});}
            var Q25;
            {var subQ0=sQuery(id+"F0.wireOp",EDGE,"E0.bottom");var subQ1=sQuery(id+"F6.wireOp",EDGE,"E8.top");var subQ2=sQuery(id+"F6.wireOp",EDGE,"E7.right");var subQ3=makeQuery(id+"F6.imprint","INTERSECT",VERTEX,{"derivedFrom":[subQ2,subQ1]});Q25=makeQuery(id+"F7.boolean.opBoolean","SPLIT",FACE,{"disambiguationData":[TD([makeQuery(id+"F7.opExtrude","SWEPT_FACE",FACE,{"disambiguationData":[OSD([subQ1]),TDD([makeQuery(id+"F6.imprint","IMPRINT",EDGE,{"disambiguationData":[TD([[subQ3,-1.0]])],"derivedFrom":subQ1})])]})])],"derivedFrom":makeQuery(id+"F4.opShell","OFFSET_FACE",FACE,{"disambiguationData":[OSD([subQ0,sQuery(id+"F0.wireOp",EDGE,"E0.top"),sQuery(id+"F0.wireOp",EDGE,"E0.left"),sQuery(id+"F0.wireOp",EDGE,"E0.right")])]})});}
            var Q26;
            {var subQ0=sQuery(id+"F0.wireOp",EDGE,"E0.bottom");var subQ1=sQuery(id+"F0.wireOp",EDGE,"E0.left");var subQ6=sQuery(id+"F2.wireOp",EDGE,"E1.bottom");Q26=makeQuery(id+"F7.boolean.opBoolean","SPLIT",FACE,{"disambiguationData":[TD([makeQuery(id+"F4.opShell","OFFSET_FACE",FACE,{"disambiguationData":[OSD([subQ6]),TDD([makeQuery(id+"Fj79t6Fnd16a4gd_1.1.F3.boolean.opBoolean","COPY",FACE,{"derivedFrom":makeQuery(id+"Fj79t6Fnd16a4gd_1.1.F3.opExtrude","SWEPT_FACE",FACE,{"disambiguationData":[OSD([subQ6])]})})])]})])],"derivedFrom":makeQuery(id+"F4.opShell","OFFSET_FACE",FACE,{"disambiguationData":[OSD([subQ0,sQuery(id+"F0.wireOp",EDGE,"E0.top"),subQ1,sQuery(id+"F0.wireOp",EDGE,"E0.right")])]})});}
            var Q27;
            {var subQ0=sQuery(id+"F0.wireOp",EDGE,"E0.top");var subQ1=sQuery(id+"F0.wireOp",EDGE,"E0.left");var subQ3=sQuery(id+"F2.wireOp",EDGE,"E1.top");Q27=makeQuery(id+"F7.boolean.opBoolean","SPLIT",FACE,{"disambiguationData":[TD([makeQuery(id+"F4.opShell","OFFSET_FACE",FACE,{"disambiguationData":[OSD([subQ3]),TDD([makeQuery(id+"Fj79t6Fnd16a4gd_1.1.F3.boolean.opBoolean","COPY",FACE,{"derivedFrom":makeQuery(id+"Fj79t6Fnd16a4gd_1.1.F3.opExtrude","SWEPT_FACE",FACE,{"disambiguationData":[OSD([subQ3])]})})])]})])],"derivedFrom":makeQuery(id+"F4.opShell","OFFSET_FACE",FACE,{"disambiguationData":[OSD([sQuery(id+"F0.wireOp",EDGE,"E0.bottom"),subQ0,subQ1,sQuery(id+"F0.wireOp",EDGE,"E0.right")])]})});}
            var Q28;
            {var subQ0=sQuery(id+"F0.wireOp",EDGE,"E0.top");var subQ1=sQuery(id+"F6.wireOp",EDGE,"E8.bottom");var subQ2=sQuery(id+"F6.wireOp",EDGE,"E7.right");var subQ3=makeQuery(id+"F6.imprint","INTERSECT",VERTEX,{"derivedFrom":[subQ2,subQ1]});Q28=makeQuery(id+"F7.boolean.opBoolean","SPLIT",FACE,{"disambiguationData":[TD([makeQuery(id+"F7.opExtrude","SWEPT_FACE",FACE,{"disambiguationData":[OSD([subQ1]),TDD([makeQuery(id+"F6.imprint","IMPRINT",EDGE,{"disambiguationData":[TD([[subQ3,-1.0]])],"derivedFrom":subQ1})])]})])],"derivedFrom":makeQuery(id+"F4.opShell","OFFSET_FACE",FACE,{"disambiguationData":[OSD([sQuery(id+"F0.wireOp",EDGE,"E0.bottom"),subQ0,sQuery(id+"F0.wireOp",EDGE,"E0.left"),sQuery(id+"F0.wireOp",EDGE,"E0.right")])]})});}
            var Q29;
            {var subQ0=sQuery(id+"F0.wireOp",EDGE,"E0.top");var subQ5=sQuery(id+"F0.wireOp",EDGE,"E0.right");var subQ7=sQuery(id+"F2.wireOp",EDGE,"E1.top");Q29=makeQuery(id+"F7.boolean.opBoolean","SPLIT",FACE,{"disambiguationData":[TD([makeQuery(id+"F4.opShell","OFFSET_FACE",FACE,{"disambiguationData":[OSD([subQ7]),TDD([makeQuery(id+"F3.boolean.opBoolean","COPY",FACE,{"derivedFrom":makeQuery(id+"F3.opExtrude","SWEPT_FACE",FACE,{"disambiguationData":[OSD([subQ7])]})})])]})])],"derivedFrom":makeQuery(id+"F4.opShell","OFFSET_FACE",FACE,{"disambiguationData":[OSD([sQuery(id+"F0.wireOp",EDGE,"E0.bottom"),subQ0,sQuery(id+"F0.wireOp",EDGE,"E0.left"),subQ5])]})});}
            var Q30;
            {var subQ0=sQuery(id+"F6.wireOp",EDGE,"E9.right");var subQ1=sQuery(id+"F0.wireOp",EDGE,"E0.bottom");Q30=makeQuery(id+"F7.opExtrude","TWEAK_EDGE",EDGE,{"derivedFrom":[makeQuery(id+"F4.opShell","OFFSET_FACE",FACE,{"disambiguationData":[OSD([subQ1])]}),makeQuery(id+"F6.imprint","IMPRINT",EDGE,{"disambiguationData":[TD([[makeQuery(id+"F6.imprint","INTERSECT",VERTEX,{"derivedFrom":[sQuery(id+"F6.wireOp",EDGE,"E8.top"),subQ0]}),1.0]])],"derivedFrom":subQ0})]});}
            var Q31;
            {var subQ0=sQuery(id+"F6.wireOp",EDGE,"E9.left");var subQ1=sQuery(id+"F0.wireOp",EDGE,"E0.bottom");Q31=makeQuery(id+"F7.opExtrude","TWEAK_EDGE",EDGE,{"derivedFrom":[makeQuery(id+"F4.opShell","OFFSET_FACE",FACE,{"disambiguationData":[OSD([subQ1])]}),makeQuery(id+"F6.imprint","IMPRINT",EDGE,{"disambiguationData":[TD([[makeQuery(id+"F6.imprint","INTERSECT",VERTEX,{"derivedFrom":[sQuery(id+"F6.wireOp",EDGE,"E8.top"),subQ0]}),1.0]])],"derivedFrom":subQ0})]});}
            var Q32;
            {var subQ0=sQuery(id+"F6.wireOp",EDGE,"E7.right");var subQ1=sQuery(id+"F0.wireOp",EDGE,"E0.bottom");Q32=makeQuery(id+"F7.opExtrude","TWEAK_EDGE",EDGE,{"derivedFrom":[makeQuery(id+"F4.opShell","OFFSET_FACE",FACE,{"disambiguationData":[OSD([subQ1])]}),makeQuery(id+"F6.imprint","IMPRINT",EDGE,{"disambiguationData":[TD([[makeQuery(id+"F6.imprint","INTERSECT",VERTEX,{"derivedFrom":[subQ0,sQuery(id+"F6.wireOp",EDGE,"E8.top")]}),1.0]])],"derivedFrom":subQ0})]});}
            var Q33;
            {var subQ0=sQuery(id+"F6.wireOp",EDGE,"E7.left");var subQ1=sQuery(id+"F0.wireOp",EDGE,"E0.bottom");Q33=makeQuery(id+"F7.opExtrude","TWEAK_EDGE",EDGE,{"derivedFrom":[makeQuery(id+"F4.opShell","OFFSET_FACE",FACE,{"disambiguationData":[OSD([subQ1])]}),makeQuery(id+"F6.imprint","IMPRINT",EDGE,{"disambiguationData":[TD([[makeQuery(id+"F6.imprint","INTERSECT",VERTEX,{"derivedFrom":[subQ0,sQuery(id+"F6.wireOp",EDGE,"E8.top")]}),1.0]])],"derivedFrom":subQ0})]});}
            var Q34;
            {var subQ0=sQuery(id+"F6.wireOp",EDGE,"E9.right");var subQ1=sQuery(id+"F0.wireOp",EDGE,"E0.top");Q34=makeQuery(id+"F7.opExtrude","TWEAK_EDGE",EDGE,{"derivedFrom":[makeQuery(id+"F4.opShell","OFFSET_FACE",FACE,{"disambiguationData":[OSD([subQ1])]}),makeQuery(id+"F6.imprint","IMPRINT",EDGE,{"disambiguationData":[TD([[makeQuery(id+"F6.imprint","INTERSECT",VERTEX,{"derivedFrom":[sQuery(id+"F6.wireOp",EDGE,"E8.bottom"),subQ0]}),-1.0]])],"derivedFrom":subQ0})]});}
            var Q35;
            {var subQ0=sQuery(id+"F6.wireOp",EDGE,"E7.right");var subQ1=sQuery(id+"F0.wireOp",EDGE,"E0.top");Q35=makeQuery(id+"F7.opExtrude","TWEAK_EDGE",EDGE,{"derivedFrom":[makeQuery(id+"F4.opShell","OFFSET_FACE",FACE,{"disambiguationData":[OSD([subQ1])]}),makeQuery(id+"F6.imprint","IMPRINT",EDGE,{"disambiguationData":[TD([[makeQuery(id+"F6.imprint","INTERSECT",VERTEX,{"derivedFrom":[subQ0,sQuery(id+"F6.wireOp",EDGE,"E8.bottom")]}),-1.0]])],"derivedFrom":subQ0})]});}
            var Q36;
            {var subQ0=sQuery(id+"F6.wireOp",EDGE,"E9.left");var subQ1=sQuery(id+"F0.wireOp",EDGE,"E0.top");Q36=makeQuery(id+"F7.opExtrude","TWEAK_EDGE",EDGE,{"derivedFrom":[makeQuery(id+"F4.opShell","OFFSET_FACE",FACE,{"disambiguationData":[OSD([subQ1])]}),makeQuery(id+"F6.imprint","IMPRINT",EDGE,{"disambiguationData":[TD([[makeQuery(id+"F6.imprint","INTERSECT",VERTEX,{"derivedFrom":[sQuery(id+"F6.wireOp",EDGE,"E8.bottom"),subQ0]}),-1.0]])],"derivedFrom":subQ0})]});}
            var Q37;
            {var subQ0=sQuery(id+"F6.wireOp",EDGE,"E7.left");var subQ1=sQuery(id+"F0.wireOp",EDGE,"E0.top");Q37=makeQuery(id+"F7.opExtrude","TWEAK_EDGE",EDGE,{"derivedFrom":[makeQuery(id+"F4.opShell","OFFSET_FACE",FACE,{"disambiguationData":[OSD([subQ1])]}),makeQuery(id+"F6.imprint","IMPRINT",EDGE,{"disambiguationData":[TD([[makeQuery(id+"F6.imprint","INTERSECT",VERTEX,{"derivedFrom":[subQ0,sQuery(id+"F6.wireOp",EDGE,"E8.bottom")]}),-1.0]])],"derivedFrom":subQ0})]});}
            var Q38;
            {var subQ0=sQuery(id+"F6.wireOp",EDGE,"E12.right");var subQ1=sQuery(id+"F0.wireOp",EDGE,"E0.bottom");Q38=makeQuery(id+"F7.opExtrude","TWEAK_EDGE",EDGE,{"derivedFrom":[makeQuery(id+"F4.opShell","OFFSET_FACE",FACE,{"disambiguationData":[OSD([subQ1])]}),makeQuery(id+"F6.imprint","IMPRINT",EDGE,{"disambiguationData":[TD([[makeQuery(id+"F6.imprint","INTERSECT",VERTEX,{"derivedFrom":[sQuery(id+"F6.wireOp",EDGE,"E8.top"),subQ0]}),1.0]])],"derivedFrom":subQ0})]});}
            var Q39;
            Q39=makeQuery(id+"F7.opExtrude","SWEPT_EDGE",EDGE,{"disambiguationData":[OSD([sQuery(id+"F6.wireOp",EDGE,"E8.bottom"),sQuery(id+"F6.wireOp",EDGE,"E12.right")])]});
            var Q40;
            Q40=makeQuery(id+"F7.opExtrude","SWEPT_EDGE",EDGE,{"disambiguationData":[OSD([sQuery(id+"F6.wireOp",EDGE,"E8.bottom"),sQuery(id+"F6.wireOp",EDGE,"E9.right")])]});
            var Q41;
            Q41=makeQuery(id+"F7.opExtrude","SWEPT_EDGE",EDGE,{"disambiguationData":[OSD([sQuery(id+"F6.wireOp",EDGE,"E7.right"),sQuery(id+"F6.wireOp",EDGE,"E8.bottom")])]});
            var Q42;
            Q42=makeQuery(id+"F7.opExtrude","SWEPT_EDGE",EDGE,{"disambiguationData":[OSD([sQuery(id+"F6.wireOp",EDGE,"E8.bottom"),sQuery(id+"F6.wireOp",EDGE,"E13.right")])]});
            var Q43;
            {var subQ0=sQuery(id+"F6.wireOp",EDGE,"E13.right");var subQ1=sQuery(id+"F0.wireOp",EDGE,"E0.bottom");Q43=makeQuery(id+"F7.opExtrude","TWEAK_EDGE",EDGE,{"derivedFrom":[makeQuery(id+"F4.opShell","OFFSET_FACE",FACE,{"disambiguationData":[OSD([subQ1])]}),makeQuery(id+"F6.imprint","IMPRINT",EDGE,{"disambiguationData":[TD([[makeQuery(id+"F6.imprint","INTERSECT",VERTEX,{"derivedFrom":[sQuery(id+"F6.wireOp",EDGE,"E8.top"),subQ0]}),1.0]])],"derivedFrom":subQ0})]});}
            var Q44;
            {var subQ0=sQuery(id+"F6.wireOp",EDGE,"E13.left");var subQ1=sQuery(id+"F0.wireOp",EDGE,"E0.bottom");Q44=makeQuery(id+"F7.opExtrude","TWEAK_EDGE",EDGE,{"derivedFrom":[makeQuery(id+"F4.opShell","OFFSET_FACE",FACE,{"disambiguationData":[OSD([subQ1])]}),makeQuery(id+"F6.imprint","IMPRINT",EDGE,{"disambiguationData":[TD([[makeQuery(id+"F6.imprint","INTERSECT",VERTEX,{"derivedFrom":[sQuery(id+"F6.wireOp",EDGE,"E8.top"),subQ0]}),1.0]])],"derivedFrom":subQ0})]});}
            var Q45;
            Q45=makeQuery(id+"F7.opExtrude","SWEPT_EDGE",EDGE,{"disambiguationData":[OSD([sQuery(id+"F6.wireOp",EDGE,"E8.bottom"),sQuery(id+"F6.wireOp",EDGE,"E13.left")])]});
            var Q46;
            Q46=makeQuery(id+"F7.opExtrude","SWEPT_EDGE",EDGE,{"disambiguationData":[OSD([sQuery(id+"F6.wireOp",EDGE,"E7.left"),sQuery(id+"F6.wireOp",EDGE,"E8.bottom")])]});
            var Q47;
            Q47=makeQuery(id+"F7.opExtrude","SWEPT_EDGE",EDGE,{"disambiguationData":[OSD([sQuery(id+"F6.wireOp",EDGE,"E8.bottom"),sQuery(id+"F6.wireOp",EDGE,"E9.left")])]});
            var Q48;
            Q48=makeQuery(id+"F7.opExtrude","SWEPT_EDGE",EDGE,{"disambiguationData":[OSD([sQuery(id+"F6.wireOp",EDGE,"E8.bottom"),sQuery(id+"F6.wireOp",EDGE,"E12.left")])]});
            var Q49;
            {var subQ0=sQuery(id+"F6.wireOp",EDGE,"E12.left");var subQ1=sQuery(id+"F0.wireOp",EDGE,"E0.bottom");Q49=makeQuery(id+"F7.opExtrude","TWEAK_EDGE",EDGE,{"derivedFrom":[makeQuery(id+"F4.opShell","OFFSET_FACE",FACE,{"disambiguationData":[OSD([subQ1])]}),makeQuery(id+"F6.imprint","IMPRINT",EDGE,{"disambiguationData":[TD([[makeQuery(id+"F6.imprint","INTERSECT",VERTEX,{"derivedFrom":[sQuery(id+"F6.wireOp",EDGE,"E8.top"),subQ0]}),1.0]])],"derivedFrom":subQ0})]});}
            var Q50;
            {var subQ0=sQuery(id+"F6.wireOp",EDGE,"E8.bottom");var subQ1=sQuery(id+"F0.wireOp",EDGE,"E0.right");Q50=makeQuery(id+"F7.opExtrude","TWEAK_EDGE",EDGE,{"derivedFrom":[makeQuery(id+"F4.opShell","OFFSET_FACE",FACE,{"disambiguationData":[OSD([subQ1])]}),makeQuery(id+"F6.imprint","IMPRINT",EDGE,{"disambiguationData":[TD([[makeQuery(id+"F6.imprint","INTERSECT",VERTEX,{"derivedFrom":[subQ0,sQuery(id+"F6.wireOp",EDGE,"E12.right")]}),-1.0]])],"derivedFrom":subQ0})]});}
            var Q51;
            {var subQ2=sQuery(id+"F0.wireOp",EDGE,"E0.right");var subQ5=sQuery(id+"F0.wireOp",EDGE,"E0.bottom");var subQ6=sQuery(id+"F2.wireOp",EDGE,"E1.bottom");var subQ9=sQuery(id+"F2.wireOp",EDGE,"E2.left");Q51=makeQuery(id+"F8.opFillet","BLEND_EDGE",EDGE,{"blendedFrom":[makeQuery(id+"F7.boolean.opBoolean","SPLIT",EDGE,{"disambiguationData":[TD([makeQuery(id+"F4.opShell","OFFSET_FACE",FACE,{"disambiguationData":[OSD([subQ9]),TDD([makeQuery(id+"F3.boolean.opBoolean","COPY",FACE,{"derivedFrom":makeQuery(id+"F3.opExtrude","SWEPT_FACE",FACE,{"disambiguationData":[OSD([subQ9]),TDD([makeQuery(id+"F2.imprint","IMPRINT",EDGE,{"disambiguationData":[TD([[makeQuery(id+"F2.imprint","INTERSECT",VERTEX,{"derivedFrom":[subQ6,subQ9]}),1.0]])],"derivedFrom":subQ9})])]})})])]})])],"derivedFrom":makeQuery(id+"F4.opShell","OFFSET_EDGE",EDGE,{"disambiguationData":[OSD([subQ5]),TDD([makeQuery(id+"F1.opExtrude","CAP_EDGE",EDGE,{"disambiguationData":[OSD([subQ5])],"isStart":false})])]})}),makeQuery(id+"F7.boolean.opBoolean","SPLIT",FACE,{"disambiguationData":[TD([makeQuery(id+"F4.opShell","OFFSET_FACE",FACE,{"disambiguationData":[OSD([subQ6]),TDD([makeQuery(id+"F3.boolean.opBoolean","COPY",FACE,{"derivedFrom":makeQuery(id+"F3.opExtrude","SWEPT_FACE",FACE,{"disambiguationData":[OSD([subQ6])]})})])]})])],"derivedFrom":makeQuery(id+"F4.opShell","OFFSET_FACE",FACE,{"disambiguationData":[OSD([subQ2])]})})],"blendedInto":[makeQuery(id+"F7.boolean.opBoolean","SPLIT",FACE,{"disambiguationData":[TD([makeQuery(id+"F4.opShell","OFFSET_FACE",FACE,{"disambiguationData":[OSD([subQ6]),TDD([makeQuery(id+"F3.boolean.opBoolean","COPY",FACE,{"derivedFrom":makeQuery(id+"F3.opExtrude","SWEPT_FACE",FACE,{"disambiguationData":[OSD([subQ6])]})})])]})])],"derivedFrom":makeQuery(id+"F4.opShell","OFFSET_FACE",FACE,{"disambiguationData":[OSD([subQ2])]})})]});}
            var Q52;
            {var subQ0=sQuery(id+"F6.wireOp",EDGE,"E13.left");var subQ1=sQuery(id+"F6.wireOp",EDGE,"E8.bottom");var subQ2=sQuery(id+"F0.wireOp",EDGE,"E0.right");var subQ3=sQuery(id+"F0.wireOp",EDGE,"E0.left");var subQ4=sQuery(id+"F0.wireOp",EDGE,"E0.top");var subQ5=sQuery(id+"F0.wireOp",EDGE,"E0.bottom");var subQ6=sQuery(id+"F2.wireOp",EDGE,"E1.top");var subQ7=makeQuery(id+"F4.opShell","OFFSET_FACE",FACE,{"disambiguationData":[OSD([subQ5,subQ4,subQ3,subQ2])]});var subQ8=makeQuery(id+"F6.imprint","IMPRINT",EDGE,{"disambiguationData":[TD([[makeQuery(id+"F6.imprint","INTERSECT",VERTEX,{"derivedFrom":[subQ1,subQ0]}),1.0]])],"derivedFrom":subQ1});Q52=makeQuery(id+"F8.opFillet","BLEND_EDGE",EDGE,{"blendedFrom":[makeQuery(id+"F7.opExtrude","TWEAK_EDGE",EDGE,{"derivedFrom":[subQ7,subQ8]}),makeQuery(id+"F7.boolean.opBoolean","SPLIT",FACE,{"disambiguationData":[TD([makeQuery(id+"F4.opShell","OFFSET_FACE",FACE,{"disambiguationData":[OSD([subQ6]),TDD([makeQuery(id+"Fj79t6Fnd16a4gd_1.1.F3.boolean.opBoolean","COPY",FACE,{"derivedFrom":makeQuery(id+"Fj79t6Fnd16a4gd_1.1.F3.opExtrude","SWEPT_FACE",FACE,{"disambiguationData":[OSD([subQ6])]})})])]})])],"derivedFrom":makeQuery(id+"F4.opShell","OFFSET_FACE",FACE,{"disambiguationData":[OSD([subQ3])]})})],"blendedInto":[makeQuery(id+"F7.boolean.opBoolean","SPLIT",FACE,{"disambiguationData":[TD([makeQuery(id+"F4.opShell","OFFSET_FACE",FACE,{"disambiguationData":[OSD([subQ6]),TDD([makeQuery(id+"Fj79t6Fnd16a4gd_1.1.F3.boolean.opBoolean","COPY",FACE,{"derivedFrom":makeQuery(id+"Fj79t6Fnd16a4gd_1.1.F3.opExtrude","SWEPT_FACE",FACE,{"disambiguationData":[OSD([subQ6])]})})])]})])],"derivedFrom":makeQuery(id+"F4.opShell","OFFSET_FACE",FACE,{"disambiguationData":[OSD([subQ3])]})})]});}
            var Q53;
            {var subQ0=sQuery(id+"F6.wireOp",EDGE,"E13.left");var subQ1=sQuery(id+"F6.wireOp",EDGE,"E8.top");var subQ2=sQuery(id+"F0.wireOp",EDGE,"E0.right");var subQ3=sQuery(id+"F0.wireOp",EDGE,"E0.left");var subQ4=sQuery(id+"F0.wireOp",EDGE,"E0.top");var subQ5=sQuery(id+"F0.wireOp",EDGE,"E0.bottom");var subQ6=sQuery(id+"F2.wireOp",EDGE,"E1.bottom");var subQ7=makeQuery(id+"F4.opShell","OFFSET_FACE",FACE,{"disambiguationData":[OSD([subQ5,subQ4,subQ3,subQ2])]});var subQ8=makeQuery(id+"F6.imprint","IMPRINT",EDGE,{"disambiguationData":[TD([[makeQuery(id+"F6.imprint","INTERSECT",VERTEX,{"derivedFrom":[subQ1,subQ0]}),1.0]])],"derivedFrom":subQ1});Q53=makeQuery(id+"F8.opFillet","BLEND_EDGE",EDGE,{"blendedFrom":[makeQuery(id+"F7.opExtrude","TWEAK_EDGE",EDGE,{"derivedFrom":[subQ7,subQ8]}),makeQuery(id+"F7.boolean.opBoolean","SPLIT",FACE,{"disambiguationData":[TD([makeQuery(id+"F4.opShell","OFFSET_FACE",FACE,{"disambiguationData":[OSD([subQ6]),TDD([makeQuery(id+"Fj79t6Fnd16a4gd_1.1.F3.boolean.opBoolean","COPY",FACE,{"derivedFrom":makeQuery(id+"Fj79t6Fnd16a4gd_1.1.F3.opExtrude","SWEPT_FACE",FACE,{"disambiguationData":[OSD([subQ6])]})})])]})])],"derivedFrom":makeQuery(id+"F4.opShell","OFFSET_FACE",FACE,{"disambiguationData":[OSD([subQ3])]})})],"blendedInto":[makeQuery(id+"F7.boolean.opBoolean","SPLIT",FACE,{"disambiguationData":[TD([makeQuery(id+"F4.opShell","OFFSET_FACE",FACE,{"disambiguationData":[OSD([subQ6]),TDD([makeQuery(id+"Fj79t6Fnd16a4gd_1.1.F3.boolean.opBoolean","COPY",FACE,{"derivedFrom":makeQuery(id+"Fj79t6Fnd16a4gd_1.1.F3.opExtrude","SWEPT_FACE",FACE,{"disambiguationData":[OSD([subQ6])]})})])]})])],"derivedFrom":makeQuery(id+"F4.opShell","OFFSET_FACE",FACE,{"disambiguationData":[OSD([subQ3])]})})]});}
            var Q54;
            {var subQ3=sQuery(id+"F0.wireOp",EDGE,"E0.left");var subQ5=sQuery(id+"F0.wireOp",EDGE,"E0.bottom");var subQ6=sQuery(id+"F2.wireOp",EDGE,"E1.bottom");var subQ9=sQuery(id+"F2.wireOp",EDGE,"E2.left");Q54=makeQuery(id+"F8.opFillet","BLEND_EDGE",EDGE,{"blendedFrom":[makeQuery(id+"F7.boolean.opBoolean","SPLIT",EDGE,{"disambiguationData":[TD([makeQuery(id+"F4.opShell","OFFSET_FACE",FACE,{"disambiguationData":[OSD([subQ9]),TDD([makeQuery(id+"Fj79t6Fnd16a4gd_1.1.F3.boolean.opBoolean","COPY",FACE,{"derivedFrom":makeQuery(id+"Fj79t6Fnd16a4gd_1.1.F3.opExtrude","SWEPT_FACE",FACE,{"disambiguationData":[OSD([subQ9]),TDD([makeQuery(id+"F2.imprint","IMPRINT",EDGE,{"disambiguationData":[TD([[makeQuery(id+"F2.imprint","INTERSECT",VERTEX,{"derivedFrom":[subQ6,subQ9]}),1.0]])],"derivedFrom":subQ9})])]})})])]})])],"derivedFrom":makeQuery(id+"F4.opShell","OFFSET_EDGE",EDGE,{"disambiguationData":[OSD([subQ5]),TDD([makeQuery(id+"F1.opExtrude","CAP_EDGE",EDGE,{"disambiguationData":[OSD([subQ5])],"isStart":false})])]})}),makeQuery(id+"F7.boolean.opBoolean","SPLIT",FACE,{"disambiguationData":[TD([makeQuery(id+"F4.opShell","OFFSET_FACE",FACE,{"disambiguationData":[OSD([subQ6]),TDD([makeQuery(id+"Fj79t6Fnd16a4gd_1.1.F3.boolean.opBoolean","COPY",FACE,{"derivedFrom":makeQuery(id+"Fj79t6Fnd16a4gd_1.1.F3.opExtrude","SWEPT_FACE",FACE,{"disambiguationData":[OSD([subQ6])]})})])]})])],"derivedFrom":makeQuery(id+"F4.opShell","OFFSET_FACE",FACE,{"disambiguationData":[OSD([subQ3])]})})],"blendedInto":[makeQuery(id+"F7.boolean.opBoolean","SPLIT",FACE,{"disambiguationData":[TD([makeQuery(id+"F4.opShell","OFFSET_FACE",FACE,{"disambiguationData":[OSD([subQ6]),TDD([makeQuery(id+"Fj79t6Fnd16a4gd_1.1.F3.boolean.opBoolean","COPY",FACE,{"derivedFrom":makeQuery(id+"Fj79t6Fnd16a4gd_1.1.F3.opExtrude","SWEPT_FACE",FACE,{"disambiguationData":[OSD([subQ6])]})})])]})])],"derivedFrom":makeQuery(id+"F4.opShell","OFFSET_FACE",FACE,{"disambiguationData":[OSD([subQ3])]})})]});}
            var Q55;
            {var subQ3=sQuery(id+"F0.wireOp",EDGE,"E0.left");var subQ4=sQuery(id+"F0.wireOp",EDGE,"E0.top");var subQ6=sQuery(id+"F2.wireOp",EDGE,"E1.top");var subQ9=sQuery(id+"F2.wireOp",EDGE,"E2.left");Q55=makeQuery(id+"F8.opFillet","BLEND_EDGE",EDGE,{"blendedFrom":[makeQuery(id+"F7.boolean.opBoolean","SPLIT",EDGE,{"disambiguationData":[TD([makeQuery(id+"F4.opShell","OFFSET_FACE",FACE,{"disambiguationData":[OSD([subQ9]),TDD([makeQuery(id+"Fj79t6Fnd16a4gd_1.1.F3.boolean.opBoolean","COPY",FACE,{"derivedFrom":makeQuery(id+"Fj79t6Fnd16a4gd_1.1.F3.opExtrude","SWEPT_FACE",FACE,{"disambiguationData":[OSD([subQ9]),TDD([makeQuery(id+"F2.imprint","IMPRINT",EDGE,{"disambiguationData":[TD([[makeQuery(id+"F2.imprint","INTERSECT",VERTEX,{"derivedFrom":[subQ6,subQ9]}),-1.0]])],"derivedFrom":subQ9})])]})})])]})])],"derivedFrom":makeQuery(id+"F4.opShell","OFFSET_EDGE",EDGE,{"disambiguationData":[OSD([subQ4]),TDD([makeQuery(id+"F1.opExtrude","CAP_EDGE",EDGE,{"disambiguationData":[OSD([subQ4])],"isStart":false})])]})}),makeQuery(id+"F7.boolean.opBoolean","SPLIT",FACE,{"disambiguationData":[TD([makeQuery(id+"F4.opShell","OFFSET_FACE",FACE,{"disambiguationData":[OSD([subQ6]),TDD([makeQuery(id+"Fj79t6Fnd16a4gd_1.1.F3.boolean.opBoolean","COPY",FACE,{"derivedFrom":makeQuery(id+"Fj79t6Fnd16a4gd_1.1.F3.opExtrude","SWEPT_FACE",FACE,{"disambiguationData":[OSD([subQ6])]})})])]})])],"derivedFrom":makeQuery(id+"F4.opShell","OFFSET_FACE",FACE,{"disambiguationData":[OSD([subQ3])]})})],"blendedInto":[makeQuery(id+"F7.boolean.opBoolean","SPLIT",FACE,{"disambiguationData":[TD([makeQuery(id+"F4.opShell","OFFSET_FACE",FACE,{"disambiguationData":[OSD([subQ6]),TDD([makeQuery(id+"Fj79t6Fnd16a4gd_1.1.F3.boolean.opBoolean","COPY",FACE,{"derivedFrom":makeQuery(id+"Fj79t6Fnd16a4gd_1.1.F3.opExtrude","SWEPT_FACE",FACE,{"disambiguationData":[OSD([subQ6])]})})])]})])],"derivedFrom":makeQuery(id+"F4.opShell","OFFSET_FACE",FACE,{"disambiguationData":[OSD([subQ3])]})})]});}
            var Q56;
            {var subQ0=sQuery(id+"F6.wireOp",EDGE,"E13.left");var subQ1=sQuery(id+"F0.wireOp",EDGE,"E0.top");var subQ3=makeQuery(id+"F7.opExtrude","SWEPT_FACE",FACE,{"disambiguationData":[OSD([subQ0]),TDD([makeQuery(id+"F6.imprint","IMPRINT",EDGE,{"disambiguationData":[TD([[makeQuery(id+"F6.imprint","INTERSECT",VERTEX,{"derivedFrom":[sQuery(id+"F6.wireOp",EDGE,"E8.bottom"),subQ0]}),-1.0]])],"derivedFrom":subQ0})])]});var subQ4=sQuery(id+"F2.wireOp",EDGE,"E2.left");Q56=makeQuery(id+"F8.opFillet","BLEND_EDGE",EDGE,{"blendedFrom":[makeQuery(id+"F7.boolean.opBoolean","SPLIT",EDGE,{"disambiguationData":[TD([makeQuery(id+"F4.opShell","OFFSET_FACE",FACE,{"disambiguationData":[OSD([subQ4]),TDD([makeQuery(id+"Fj79t6Fnd16a4gd_1.1.F3.boolean.opBoolean","COPY",FACE,{"derivedFrom":makeQuery(id+"Fj79t6Fnd16a4gd_1.1.F3.opExtrude","SWEPT_FACE",FACE,{"disambiguationData":[OSD([subQ4]),TDD([makeQuery(id+"F2.imprint","IMPRINT",EDGE,{"disambiguationData":[TD([[makeQuery(id+"F2.imprint","INTERSECT",VERTEX,{"derivedFrom":[sQuery(id+"F2.wireOp",EDGE,"E1.top"),subQ4]}),-1.0]])],"derivedFrom":subQ4})])]})})])]})])],"derivedFrom":makeQuery(id+"F4.opShell","OFFSET_EDGE",EDGE,{"disambiguationData":[OSD([subQ1]),TDD([makeQuery(id+"F1.opExtrude","CAP_EDGE",EDGE,{"disambiguationData":[OSD([subQ1])],"isStart":false})])]})}),subQ3],"blendedInto":[subQ3]});}
            var Q57;
            {var subQ0=sQuery(id+"F6.wireOp",EDGE,"E12.left");var subQ1=sQuery(id+"F6.wireOp",EDGE,"E8.bottom");var subQ2=sQuery(id+"F0.wireOp",EDGE,"E0.top");var subQ4=makeQuery(id+"F7.opExtrude","SWEPT_FACE",FACE,{"disambiguationData":[OSD([subQ0]),TDD([makeQuery(id+"F6.imprint","IMPRINT",EDGE,{"disambiguationData":[TD([[makeQuery(id+"F6.imprint","INTERSECT",VERTEX,{"derivedFrom":[subQ1,subQ0]}),-1.0]])],"derivedFrom":subQ0})])]});var subQ5=sQuery(id+"F6.wireOp",EDGE,"E9.right");Q57=makeQuery(id+"F8.opFillet","BLEND_EDGE",EDGE,{"blendedFrom":[makeQuery(id+"F7.boolean.opBoolean","SPLIT",EDGE,{"disambiguationData":[TD([makeQuery(id+"F7.opExtrude","SWEPT_FACE",FACE,{"disambiguationData":[OSD([subQ5]),TDD([makeQuery(id+"F6.imprint","IMPRINT",EDGE,{"disambiguationData":[TD([[makeQuery(id+"F6.imprint","INTERSECT",VERTEX,{"derivedFrom":[subQ1,subQ5]}),-1.0]])],"derivedFrom":subQ5})])]})])],"derivedFrom":makeQuery(id+"F4.opShell","OFFSET_EDGE",EDGE,{"disambiguationData":[OSD([subQ2]),TDD([makeQuery(id+"F1.opExtrude","CAP_EDGE",EDGE,{"disambiguationData":[OSD([subQ2])],"isStart":false})])]})}),subQ4],"blendedInto":[subQ4]});}
            var Q58;
            {var subQ2=sQuery(id+"F0.wireOp",EDGE,"E0.right");var subQ4=sQuery(id+"F0.wireOp",EDGE,"E0.top");var subQ6=sQuery(id+"F2.wireOp",EDGE,"E1.top");var subQ9=sQuery(id+"F2.wireOp",EDGE,"E2.left");Q58=makeQuery(id+"F8.opFillet","BLEND_EDGE",EDGE,{"blendedFrom":[makeQuery(id+"F7.boolean.opBoolean","SPLIT",EDGE,{"disambiguationData":[TD([makeQuery(id+"F4.opShell","OFFSET_FACE",FACE,{"disambiguationData":[OSD([subQ9]),TDD([makeQuery(id+"F3.boolean.opBoolean","COPY",FACE,{"derivedFrom":makeQuery(id+"F3.opExtrude","SWEPT_FACE",FACE,{"disambiguationData":[OSD([subQ9]),TDD([makeQuery(id+"F2.imprint","IMPRINT",EDGE,{"disambiguationData":[TD([[makeQuery(id+"F2.imprint","INTERSECT",VERTEX,{"derivedFrom":[subQ6,subQ9]}),-1.0]])],"derivedFrom":subQ9})])]})})])]})])],"derivedFrom":makeQuery(id+"F4.opShell","OFFSET_EDGE",EDGE,{"disambiguationData":[OSD([subQ4]),TDD([makeQuery(id+"F1.opExtrude","CAP_EDGE",EDGE,{"disambiguationData":[OSD([subQ4])],"isStart":false})])]})}),makeQuery(id+"F7.boolean.opBoolean","SPLIT",FACE,{"disambiguationData":[TD([makeQuery(id+"F4.opShell","OFFSET_FACE",FACE,{"disambiguationData":[OSD([subQ6]),TDD([makeQuery(id+"F3.boolean.opBoolean","COPY",FACE,{"derivedFrom":makeQuery(id+"F3.opExtrude","SWEPT_FACE",FACE,{"disambiguationData":[OSD([subQ6])]})})])]})])],"derivedFrom":makeQuery(id+"F4.opShell","OFFSET_FACE",FACE,{"disambiguationData":[OSD([subQ2])]})})],"blendedInto":[makeQuery(id+"F7.boolean.opBoolean","SPLIT",FACE,{"disambiguationData":[TD([makeQuery(id+"F4.opShell","OFFSET_FACE",FACE,{"disambiguationData":[OSD([subQ6]),TDD([makeQuery(id+"F3.boolean.opBoolean","COPY",FACE,{"derivedFrom":makeQuery(id+"F3.opExtrude","SWEPT_FACE",FACE,{"disambiguationData":[OSD([subQ6])]})})])]})])],"derivedFrom":makeQuery(id+"F4.opShell","OFFSET_FACE",FACE,{"disambiguationData":[OSD([subQ2])]})})]});}
            var Q59;
            {var subQ0=sQuery(id+"F6.wireOp",EDGE,"E12.right");var subQ1=sQuery(id+"F6.wireOp",EDGE,"E8.top");var subQ2=sQuery(id+"F0.wireOp",EDGE,"E0.right");var subQ3=sQuery(id+"F0.wireOp",EDGE,"E0.left");var subQ4=sQuery(id+"F0.wireOp",EDGE,"E0.top");var subQ5=sQuery(id+"F0.wireOp",EDGE,"E0.bottom");var subQ6=sQuery(id+"F2.wireOp",EDGE,"E1.bottom");var subQ7=makeQuery(id+"F4.opShell","OFFSET_FACE",FACE,{"disambiguationData":[OSD([subQ5,subQ4,subQ3,subQ2])]});var subQ8=makeQuery(id+"F6.imprint","IMPRINT",EDGE,{"disambiguationData":[TD([[makeQuery(id+"F6.imprint","INTERSECT",VERTEX,{"derivedFrom":[subQ1,subQ0]}),-1.0]])],"derivedFrom":subQ1});Q59=makeQuery(id+"F8.opFillet","BLEND_EDGE",EDGE,{"blendedFrom":[makeQuery(id+"F7.opExtrude","TWEAK_EDGE",EDGE,{"derivedFrom":[subQ7,subQ8]}),makeQuery(id+"F7.boolean.opBoolean","SPLIT",FACE,{"disambiguationData":[TD([makeQuery(id+"F4.opShell","OFFSET_FACE",FACE,{"disambiguationData":[OSD([subQ6]),TDD([makeQuery(id+"F3.boolean.opBoolean","COPY",FACE,{"derivedFrom":makeQuery(id+"F3.opExtrude","SWEPT_FACE",FACE,{"disambiguationData":[OSD([subQ6])]})})])]})])],"derivedFrom":makeQuery(id+"F4.opShell","OFFSET_FACE",FACE,{"disambiguationData":[OSD([subQ2])]})})],"blendedInto":[makeQuery(id+"F7.boolean.opBoolean","SPLIT",FACE,{"disambiguationData":[TD([makeQuery(id+"F4.opShell","OFFSET_FACE",FACE,{"disambiguationData":[OSD([subQ6]),TDD([makeQuery(id+"F3.boolean.opBoolean","COPY",FACE,{"derivedFrom":makeQuery(id+"F3.opExtrude","SWEPT_FACE",FACE,{"disambiguationData":[OSD([subQ6])]})})])]})])],"derivedFrom":makeQuery(id+"F4.opShell","OFFSET_FACE",FACE,{"disambiguationData":[OSD([subQ2])]})})]});}
            var Q60;
            {var subQ0=sQuery(id+"F6.wireOp",EDGE,"E12.left");var subQ1=sQuery(id+"F6.wireOp",EDGE,"E8.top");var subQ2=makeQuery(id+"F6.imprint","INTERSECT",VERTEX,{"derivedFrom":[subQ1,subQ0]});var subQ3=sQuery(id+"F0.wireOp",EDGE,"E0.bottom");Q60=makeQuery(id+"F8.opFillet","BLEND_EDGE",EDGE,{"blendedFrom":[makeQuery(id+"F7.opExtrude","TWEAK_EDGE",EDGE,{"derivedFrom":[makeQuery(id+"F4.opShell","OFFSET_FACE",FACE,{"disambiguationData":[OSD([subQ3,sQuery(id+"F0.wireOp",EDGE,"E0.top"),sQuery(id+"F0.wireOp",EDGE,"E0.left"),sQuery(id+"F0.wireOp",EDGE,"E0.right")])]}),makeQuery(id+"F6.imprint","IMPRINT",EDGE,{"disambiguationData":[TD([[makeQuery(id+"F6.imprint","INTERSECT",VERTEX,{"derivedFrom":[subQ1,sQuery(id+"F6.wireOp",EDGE,"E9.right")]}),-1.0]])],"derivedFrom":subQ1})]}),makeQuery(id+"F7.opExtrude","SWEPT_FACE",FACE,{"disambiguationData":[OSD([subQ0]),TDD([makeQuery(id+"F6.imprint","IMPRINT",EDGE,{"disambiguationData":[TD([[subQ2,1.0]])],"derivedFrom":subQ0})])]})],"blendedInto":[makeQuery(id+"F7.opExtrude","SWEPT_FACE",FACE,{"disambiguationData":[OSD([subQ0]),TDD([makeQuery(id+"F6.imprint","IMPRINT",EDGE,{"disambiguationData":[TD([[subQ2,1.0]])],"derivedFrom":subQ0})])]})]});}
            var Q61;
            {var subQ0=sQuery(id+"F6.wireOp",EDGE,"E9.left");var subQ1=sQuery(id+"F6.wireOp",EDGE,"E8.top");var subQ2=makeQuery(id+"F6.imprint","INTERSECT",VERTEX,{"derivedFrom":[subQ1,subQ0]});var subQ3=sQuery(id+"F0.wireOp",EDGE,"E0.bottom");Q61=makeQuery(id+"F8.opFillet","BLEND_EDGE",EDGE,{"blendedFrom":[makeQuery(id+"F7.opExtrude","TWEAK_EDGE",EDGE,{"derivedFrom":[makeQuery(id+"F4.opShell","OFFSET_FACE",FACE,{"disambiguationData":[OSD([subQ3,sQuery(id+"F0.wireOp",EDGE,"E0.top"),sQuery(id+"F0.wireOp",EDGE,"E0.left"),sQuery(id+"F0.wireOp",EDGE,"E0.right")])]}),makeQuery(id+"F6.imprint","IMPRINT",EDGE,{"disambiguationData":[TD([[makeQuery(id+"F6.imprint","INTERSECT",VERTEX,{"derivedFrom":[sQuery(id+"F6.wireOp",EDGE,"E7.right"),subQ1]}),-1.0]])],"derivedFrom":subQ1})]}),makeQuery(id+"F7.opExtrude","SWEPT_FACE",FACE,{"disambiguationData":[OSD([subQ0]),TDD([makeQuery(id+"F6.imprint","IMPRINT",EDGE,{"disambiguationData":[TD([[subQ2,1.0]])],"derivedFrom":subQ0})])]})],"blendedInto":[makeQuery(id+"F7.opExtrude","SWEPT_FACE",FACE,{"disambiguationData":[OSD([subQ0]),TDD([makeQuery(id+"F6.imprint","IMPRINT",EDGE,{"disambiguationData":[TD([[subQ2,1.0]])],"derivedFrom":subQ0})])]})]});}
            var Q62;
            {var subQ0=sQuery(id+"F6.wireOp",EDGE,"E8.top");var subQ1=sQuery(id+"F6.wireOp",EDGE,"E7.left");var subQ2=makeQuery(id+"F6.imprint","INTERSECT",VERTEX,{"derivedFrom":[subQ1,subQ0]});var subQ3=sQuery(id+"F0.wireOp",EDGE,"E0.bottom");Q62=makeQuery(id+"F8.opFillet","BLEND_EDGE",EDGE,{"blendedFrom":[makeQuery(id+"F7.opExtrude","TWEAK_EDGE",EDGE,{"derivedFrom":[makeQuery(id+"F4.opShell","OFFSET_FACE",FACE,{"disambiguationData":[OSD([subQ3,sQuery(id+"F0.wireOp",EDGE,"E0.top"),sQuery(id+"F0.wireOp",EDGE,"E0.left"),sQuery(id+"F0.wireOp",EDGE,"E0.right")])]}),makeQuery(id+"F6.imprint","IMPRINT",EDGE,{"disambiguationData":[TD([[subQ2,1.0]])],"derivedFrom":subQ0})]}),makeQuery(id+"F7.opExtrude","SWEPT_FACE",FACE,{"disambiguationData":[OSD([subQ1]),TDD([makeQuery(id+"F6.imprint","IMPRINT",EDGE,{"disambiguationData":[TD([[subQ2,1.0]])],"derivedFrom":subQ1})])]})],"blendedInto":[makeQuery(id+"F7.opExtrude","SWEPT_FACE",FACE,{"disambiguationData":[OSD([subQ1]),TDD([makeQuery(id+"F6.imprint","IMPRINT",EDGE,{"disambiguationData":[TD([[subQ2,1.0]])],"derivedFrom":subQ1})])]})]});}
            var Q63;
            {var subQ0=sQuery(id+"F6.wireOp",EDGE,"E13.left");var subQ1=sQuery(id+"F6.wireOp",EDGE,"E8.top");var subQ2=makeQuery(id+"F6.imprint","INTERSECT",VERTEX,{"derivedFrom":[subQ1,subQ0]});var subQ3=sQuery(id+"F0.wireOp",EDGE,"E0.bottom");var subQ4=sQuery(id+"F0.wireOp",EDGE,"E0.left");Q63=makeQuery(id+"F8.opFillet","BLEND_EDGE",EDGE,{"blendedFrom":[makeQuery(id+"F7.opExtrude","TWEAK_EDGE",EDGE,{"derivedFrom":[makeQuery(id+"F4.opShell","OFFSET_FACE",FACE,{"disambiguationData":[OSD([subQ3,sQuery(id+"F0.wireOp",EDGE,"E0.top"),subQ4,sQuery(id+"F0.wireOp",EDGE,"E0.right")])]}),makeQuery(id+"F6.imprint","IMPRINT",EDGE,{"disambiguationData":[TD([[subQ2,1.0]])],"derivedFrom":subQ1})]}),makeQuery(id+"F7.opExtrude","SWEPT_FACE",FACE,{"disambiguationData":[OSD([subQ0]),TDD([makeQuery(id+"F6.imprint","IMPRINT",EDGE,{"disambiguationData":[TD([[subQ2,1.0]])],"derivedFrom":subQ0})])]})],"blendedInto":[makeQuery(id+"F7.opExtrude","SWEPT_FACE",FACE,{"disambiguationData":[OSD([subQ0]),TDD([makeQuery(id+"F6.imprint","IMPRINT",EDGE,{"disambiguationData":[TD([[subQ2,1.0]])],"derivedFrom":subQ0})])]})]});}
            var Q64;
            {var subQ0=sQuery(id+"F6.wireOp",EDGE,"E12.right");var subQ1=sQuery(id+"F6.wireOp",EDGE,"E8.top");var subQ2=makeQuery(id+"F6.imprint","INTERSECT",VERTEX,{"derivedFrom":[subQ1,subQ0]});var subQ3=sQuery(id+"F0.wireOp",EDGE,"E0.bottom");var subQ4=sQuery(id+"F0.wireOp",EDGE,"E0.right");Q64=makeQuery(id+"F8.opFillet","BLEND_EDGE",EDGE,{"blendedFrom":[makeQuery(id+"F7.opExtrude","TWEAK_EDGE",EDGE,{"derivedFrom":[makeQuery(id+"F4.opShell","OFFSET_FACE",FACE,{"disambiguationData":[OSD([subQ3,sQuery(id+"F0.wireOp",EDGE,"E0.top"),sQuery(id+"F0.wireOp",EDGE,"E0.left"),subQ4])]}),makeQuery(id+"F6.imprint","IMPRINT",EDGE,{"disambiguationData":[TD([[subQ2,-1.0]])],"derivedFrom":subQ1})]}),makeQuery(id+"F7.opExtrude","SWEPT_FACE",FACE,{"disambiguationData":[OSD([subQ0]),TDD([makeQuery(id+"F6.imprint","IMPRINT",EDGE,{"disambiguationData":[TD([[subQ2,1.0]])],"derivedFrom":subQ0})])]})],"blendedInto":[makeQuery(id+"F7.opExtrude","SWEPT_FACE",FACE,{"disambiguationData":[OSD([subQ0]),TDD([makeQuery(id+"F6.imprint","IMPRINT",EDGE,{"disambiguationData":[TD([[subQ2,1.0]])],"derivedFrom":subQ0})])]})]});}
            var Q65;
            {var subQ0=sQuery(id+"F6.wireOp",EDGE,"E12.right");var subQ1=sQuery(id+"F0.wireOp",EDGE,"E0.top");var subQ3=makeQuery(id+"F7.opExtrude","SWEPT_FACE",FACE,{"disambiguationData":[OSD([subQ0]),TDD([makeQuery(id+"F6.imprint","IMPRINT",EDGE,{"disambiguationData":[TD([[makeQuery(id+"F6.imprint","INTERSECT",VERTEX,{"derivedFrom":[sQuery(id+"F6.wireOp",EDGE,"E8.bottom"),subQ0]}),-1.0]])],"derivedFrom":subQ0})])]});var subQ4=sQuery(id+"F2.wireOp",EDGE,"E2.left");Q65=makeQuery(id+"F8.opFillet","BLEND_EDGE",EDGE,{"blendedFrom":[makeQuery(id+"F7.boolean.opBoolean","SPLIT",EDGE,{"disambiguationData":[TD([makeQuery(id+"F4.opShell","OFFSET_FACE",FACE,{"disambiguationData":[OSD([subQ4]),TDD([makeQuery(id+"F3.boolean.opBoolean","COPY",FACE,{"derivedFrom":makeQuery(id+"F3.opExtrude","SWEPT_FACE",FACE,{"disambiguationData":[OSD([subQ4]),TDD([makeQuery(id+"F2.imprint","IMPRINT",EDGE,{"disambiguationData":[TD([[makeQuery(id+"F2.imprint","INTERSECT",VERTEX,{"derivedFrom":[sQuery(id+"F2.wireOp",EDGE,"E1.top"),subQ4]}),-1.0]])],"derivedFrom":subQ4})])]})})])]})])],"derivedFrom":makeQuery(id+"F4.opShell","OFFSET_EDGE",EDGE,{"disambiguationData":[OSD([subQ1]),TDD([makeQuery(id+"F1.opExtrude","CAP_EDGE",EDGE,{"disambiguationData":[OSD([subQ1])],"isStart":false})])]})}),subQ3],"blendedInto":[subQ3]});}
            var Q66;
            {var subQ0=sQuery(id+"F6.wireOp",EDGE,"E13.right");var subQ1=sQuery(id+"F6.wireOp",EDGE,"E8.bottom");var subQ2=sQuery(id+"F0.wireOp",EDGE,"E0.top");var subQ4=makeQuery(id+"F7.opExtrude","SWEPT_FACE",FACE,{"disambiguationData":[OSD([subQ0]),TDD([makeQuery(id+"F6.imprint","IMPRINT",EDGE,{"disambiguationData":[TD([[makeQuery(id+"F6.imprint","INTERSECT",VERTEX,{"derivedFrom":[subQ1,subQ0]}),-1.0]])],"derivedFrom":subQ0})])]});var subQ5=sQuery(id+"F6.wireOp",EDGE,"E7.left");Q66=makeQuery(id+"F8.opFillet","BLEND_EDGE",EDGE,{"blendedFrom":[makeQuery(id+"F7.boolean.opBoolean","SPLIT",EDGE,{"disambiguationData":[TD([makeQuery(id+"F7.opExtrude","SWEPT_FACE",FACE,{"disambiguationData":[OSD([subQ5]),TDD([makeQuery(id+"F6.imprint","IMPRINT",EDGE,{"disambiguationData":[TD([[makeQuery(id+"F6.imprint","INTERSECT",VERTEX,{"derivedFrom":[subQ5,subQ1]}),-1.0]])],"derivedFrom":subQ5})])]})])],"derivedFrom":makeQuery(id+"F4.opShell","OFFSET_EDGE",EDGE,{"disambiguationData":[OSD([subQ2]),TDD([makeQuery(id+"F1.opExtrude","CAP_EDGE",EDGE,{"disambiguationData":[OSD([subQ2])],"isStart":false})])]})}),subQ4],"blendedInto":[subQ4]});}
            var Q67;
            {var subQ0=sQuery(id+"F6.wireOp",EDGE,"E13.right");var subQ1=sQuery(id+"F6.wireOp",EDGE,"E8.top");var subQ2=makeQuery(id+"F6.imprint","INTERSECT",VERTEX,{"derivedFrom":[subQ1,subQ0]});var subQ3=sQuery(id+"F0.wireOp",EDGE,"E0.bottom");Q67=makeQuery(id+"F8.opFillet","BLEND_EDGE",EDGE,{"blendedFrom":[makeQuery(id+"F7.opExtrude","TWEAK_EDGE",EDGE,{"derivedFrom":[makeQuery(id+"F4.opShell","OFFSET_FACE",FACE,{"disambiguationData":[OSD([subQ3,sQuery(id+"F0.wireOp",EDGE,"E0.top"),sQuery(id+"F0.wireOp",EDGE,"E0.left"),sQuery(id+"F0.wireOp",EDGE,"E0.right")])]}),makeQuery(id+"F6.imprint","IMPRINT",EDGE,{"disambiguationData":[TD([[makeQuery(id+"F6.imprint","INTERSECT",VERTEX,{"derivedFrom":[sQuery(id+"F6.wireOp",EDGE,"E7.left"),subQ1]}),1.0]])],"derivedFrom":subQ1})]}),makeQuery(id+"F7.opExtrude","SWEPT_FACE",FACE,{"disambiguationData":[OSD([subQ0]),TDD([makeQuery(id+"F6.imprint","IMPRINT",EDGE,{"disambiguationData":[TD([[subQ2,1.0]])],"derivedFrom":subQ0})])]})],"blendedInto":[makeQuery(id+"F7.opExtrude","SWEPT_FACE",FACE,{"disambiguationData":[OSD([subQ0]),TDD([makeQuery(id+"F6.imprint","IMPRINT",EDGE,{"disambiguationData":[TD([[subQ2,1.0]])],"derivedFrom":subQ0})])]})]});}
            var Q68;
            {var subQ0=sQuery(id+"F6.wireOp",EDGE,"E8.top");var subQ1=sQuery(id+"F6.wireOp",EDGE,"E7.right");var subQ2=makeQuery(id+"F6.imprint","INTERSECT",VERTEX,{"derivedFrom":[subQ1,subQ0]});var subQ3=sQuery(id+"F0.wireOp",EDGE,"E0.bottom");Q68=makeQuery(id+"F8.opFillet","BLEND_EDGE",EDGE,{"blendedFrom":[makeQuery(id+"F7.opExtrude","TWEAK_EDGE",EDGE,{"derivedFrom":[makeQuery(id+"F4.opShell","OFFSET_FACE",FACE,{"disambiguationData":[OSD([subQ3,sQuery(id+"F0.wireOp",EDGE,"E0.top"),sQuery(id+"F0.wireOp",EDGE,"E0.left"),sQuery(id+"F0.wireOp",EDGE,"E0.right")])]}),makeQuery(id+"F6.imprint","IMPRINT",EDGE,{"disambiguationData":[TD([[subQ2,-1.0]])],"derivedFrom":subQ0})]}),makeQuery(id+"F7.opExtrude","SWEPT_FACE",FACE,{"disambiguationData":[OSD([subQ1]),TDD([makeQuery(id+"F6.imprint","IMPRINT",EDGE,{"disambiguationData":[TD([[subQ2,1.0]])],"derivedFrom":subQ1})])]})],"blendedInto":[makeQuery(id+"F7.opExtrude","SWEPT_FACE",FACE,{"disambiguationData":[OSD([subQ1]),TDD([makeQuery(id+"F6.imprint","IMPRINT",EDGE,{"disambiguationData":[TD([[subQ2,1.0]])],"derivedFrom":subQ1})])]})]});}
            var Q69;
            {var subQ0=sQuery(id+"F6.wireOp",EDGE,"E9.right");var subQ1=sQuery(id+"F6.wireOp",EDGE,"E8.top");var subQ2=makeQuery(id+"F6.imprint","INTERSECT",VERTEX,{"derivedFrom":[subQ1,subQ0]});var subQ3=sQuery(id+"F0.wireOp",EDGE,"E0.bottom");Q69=makeQuery(id+"F8.opFillet","BLEND_EDGE",EDGE,{"blendedFrom":[makeQuery(id+"F7.opExtrude","TWEAK_EDGE",EDGE,{"derivedFrom":[makeQuery(id+"F4.opShell","OFFSET_FACE",FACE,{"disambiguationData":[OSD([subQ3,sQuery(id+"F0.wireOp",EDGE,"E0.top"),sQuery(id+"F0.wireOp",EDGE,"E0.left"),sQuery(id+"F0.wireOp",EDGE,"E0.right")])]}),makeQuery(id+"F6.imprint","IMPRINT",EDGE,{"disambiguationData":[TD([[subQ2,-1.0]])],"derivedFrom":subQ1})]}),makeQuery(id+"F7.opExtrude","SWEPT_FACE",FACE,{"disambiguationData":[OSD([subQ0]),TDD([makeQuery(id+"F6.imprint","IMPRINT",EDGE,{"disambiguationData":[TD([[subQ2,1.0]])],"derivedFrom":subQ0})])]})],"blendedInto":[makeQuery(id+"F7.opExtrude","SWEPT_FACE",FACE,{"disambiguationData":[OSD([subQ0]),TDD([makeQuery(id+"F6.imprint","IMPRINT",EDGE,{"disambiguationData":[TD([[subQ2,1.0]])],"derivedFrom":subQ0})])]})]});}
            fillet(context, id + "F9", {"entities" : qUnion([Q0, Q1, Q2, Q3, Q4, Q5, Q6, Q7, Q8, Q9, Q10, Q11, Q12, Q13, Q14, Q15, Q16, Q17, Q18, Q19, Q20, Q21, Q22, Q23, Q24, Q25, Q26, Q27, Q28, Q29, Q30, Q31, Q32, Q33, Q34, Q35, Q36, Q37, Q38, Q39, Q40, Q41, Q42, Q43, Q44, Q45, Q46, Q47, Q48, Q49, Q50, Q51, Q52, Q53, Q54, Q55, Q56, Q57, Q58, Q59, Q60, Q61, Q62, Q63, Q64, Q65, Q66, Q67, Q68, Q69]), "radius" : .5 * mm, "tangentPropagation" : true, "allowEdgeOverflow" : false});
        }
    });
